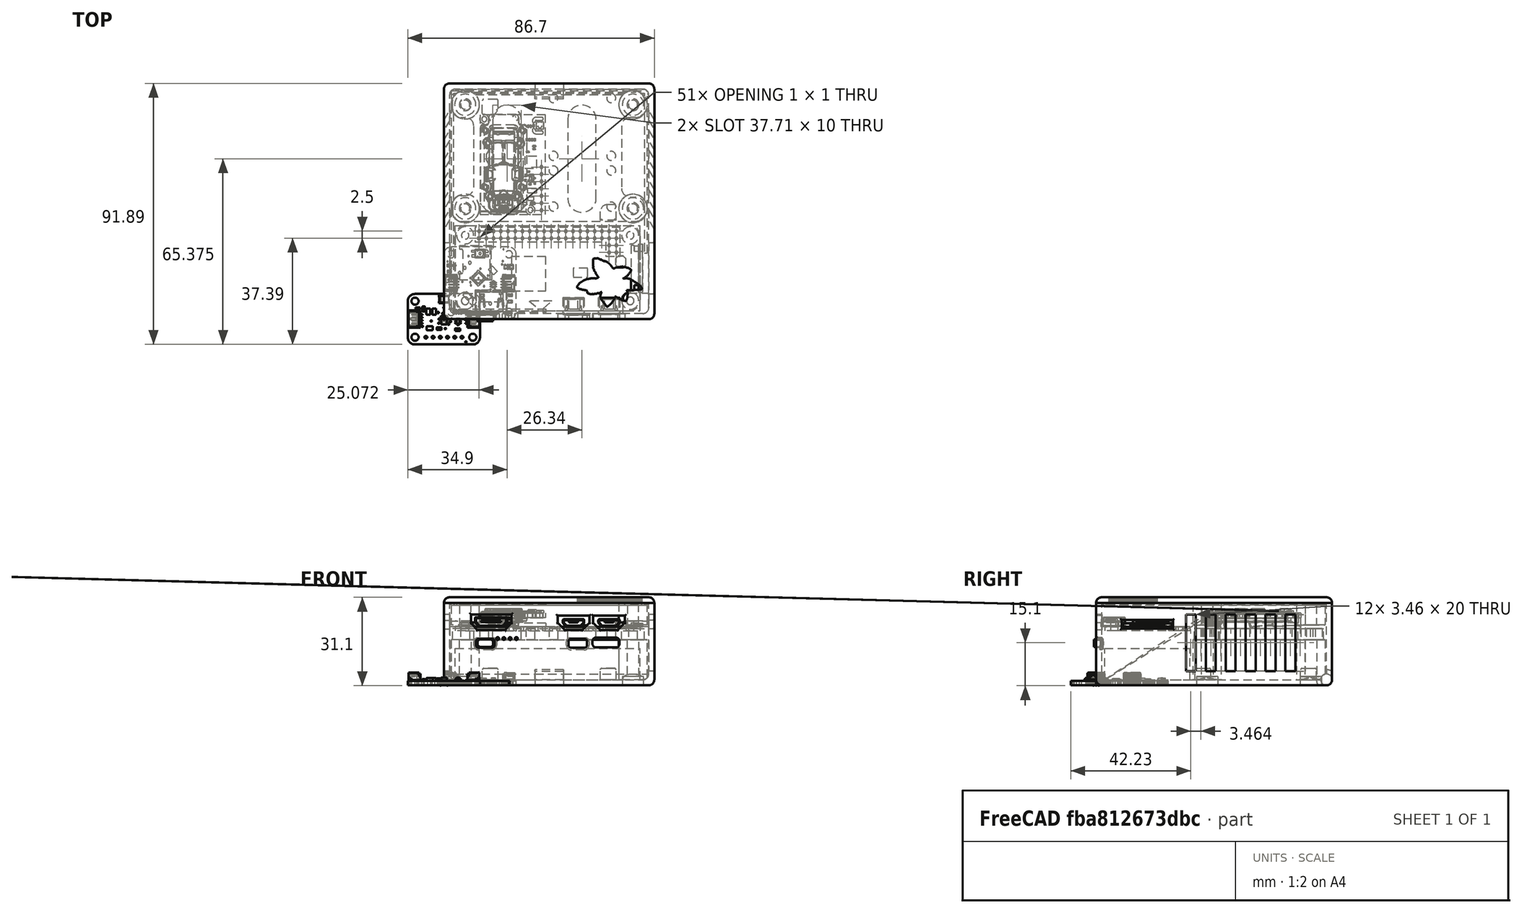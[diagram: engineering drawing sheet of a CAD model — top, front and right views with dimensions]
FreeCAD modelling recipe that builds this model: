
FCSTD DOCUMENT  (FreeCAD 0.20R29410 (Git))
Label: wearableV5_May_1_m3_2023
License: All rights reserved
LicenseURL: http://en.wikipedia.org/wiki/All_rights_reserved
objects: Part::Feature×60, Part::Cylinder×20, Part::MultiFuse×17, Sketcher::SketchObject×15, Part::Extrusion×14, App::Part×9, Part::Fillet×7, Part::Box×4, Part::Cut×4, Mesh::Feature×2, Part::Compound×1
note: 142 computed .brp shape members not serialized (recipe doc carries the construction recipe); baked Part::Feature solids carry a one-line shape summary decoded from their .brp

FEATURE [Part::Box] Box  label="battery"
  AttacherType = Attacher::AttachEngine3D
  Height = 11
  Length = 65
  Placement = pos=(4,3,2) rot=(0,0,1;0rad)
  Width = 30
FEATURE [Mesh::Feature] pisugar3Board
  Placement = pos=(-2.89,36.08,0.25) rot=(-1,0,0;4.71239rad)
FEATURE [Part::Feature] Part__Feature001  label="RaspberryPiZeroW"
  Placement = pos=(36.5,18,19.18) rot=(1,0,0;1.5708rad)
  shape: bbox 65.9 x 31.25 x 4.8 mm, 368 faces, 2 solids (baked)
FEATURE [Part::Feature] Part__Feature  label="ips7100"
  Placement = pos=(-24,0,222) rot=(0.999993,-0.003655,0;3.14159rad)
  shape: bbox 48.14 x 14.05 x 44.14 mm, 1935 faces (baked)
FEATURE [Part::Compound] Compound  label="ips7100s"
  Links = -> [Part__Feature]
  Placement = pos=(13.15,34,15.79) rot=(0,0.707107,0.707107;3.15032rad)
FEATURE [Part::Feature] Part__Feature002  label="Printed Circuit Board"
  shape: bbox 25.4 x 17.78 x 1.6 mm, 42 faces (baked)
FEATURE [Part::Feature] Part__Feature003  label="EAHC2835WD6"
  shape: bbox 3.513 x 2.813 x 0.7485 mm, 108 faces, 4 solids (baked)
FEATURE [Part::Feature] Part__Feature004  label="AS7341 v2"
  Placement = pos=(0,-0.339822,1.6) rot=(0,0,1;0rad)
  shape: bbox 2 x 3.1 x 1.1 mm, 267 faces, 26 solids (baked)
FEATURE [Part::Feature] Part__Feature005  label="CAPC-0805-T0.95-BN v1"
  Placement = pos=(-5.01759,-3.15294,1.6) rot=(0,0,1;0rad)
  shape: bbox 2.1 x 1.35 x 0.95 mm, 42 faces (baked)
FEATURE [Part::Feature] Part__Feature006  label="CAPC-0805-T0.95-BN v002"
  Placement = pos=(-5.48627,2.66154,1.6) rot=(0,0,-1;1.5708rad)
  shape: bbox 1.35 x 2.1 x 0.95 mm, 42 faces (baked)
FEATURE [Part::Feature] Part__Feature007  label="CAPC-0805-T0.95-BN v003"
  Placement = pos=(-3.43627,2.66154,1.6) rot=(0,0,-1;1.5708rad)
  shape: bbox 1.35 x 2.1 x 0.95 mm, 42 faces (baked)
FEATURE [Part::Feature] Part__Feature008  label="CAPC-0603-T0.9-BN v1"
  Placement = pos=(-1.69987,-3.28475,1.6) rot=(0,0,1;0rad)
  shape: bbox 1.7 x 0.9 x 0.9 mm, 42 faces (baked)
FEATURE [Part::Feature] Part__Feature009  label="BODY_MF06A"
  Placement = pos=(0,0,0.762) rot=(0.57735,-0.57735,-0.57735;2.0944rad)
  shape: bbox 1.601 x 2.921 x 1.016 mm, 42 faces (baked)
FEATURE [Part::Feature] Part__Feature010  label="LEAD_MF06A"
  Placement = pos=(-0.9652,-0.9525,0.1016) rot=(0.57735,-0.57735,-0.57735;2.0944rad)
  shape: bbox 0.6223 x 0.3749 x 0.8636 mm, 14 faces (baked)
FEATURE [Part::Feature] Part__Feature011  label="LEAD_MF06A001"
  Placement = pos=(-0.9652,0,0.1016) rot=(0.57735,-0.57735,-0.57735;2.0944rad)
  shape: bbox 0.6223 x 0.3749 x 0.8636 mm, 14 faces (baked)
FEATURE [Part::Feature] Part__Feature012  label="LEAD_MF06A002"
  Placement = pos=(-0.9652,0.9525,0.1016) rot=(0.57735,-0.57735,-0.57735;2.0944rad)
  shape: bbox 0.6223 x 0.3749 x 0.8636 mm, 14 faces (baked)
FEATURE [Part::Feature] Part__Feature013  label="LEAD_MF06A003"
  Placement = pos=(0.9652,-0.9525,0.1016) rot=(0.57735,0.57735,0.57735;2.0944rad)
  shape: bbox 0.6223 x 0.3749 x 0.8636 mm, 14 faces (baked)
FEATURE [Part::Feature] Part__Feature014  label="LEAD_MF06A004"
  Placement = pos=(0.9652,0,0.1016) rot=(0.57735,0.57735,0.57735;2.0944rad)
  shape: bbox 0.6223 x 0.3749 x 0.8636 mm, 14 faces (baked)
FEATURE [Part::Feature] Part__Feature015  label="LEAD_MF06A005"
  Placement = pos=(0.9652,0.9525,0.1016) rot=(0.57735,0.57735,0.57735;2.0944rad)
  shape: bbox 0.6223 x 0.3749 x 0.8636 mm, 14 faces (baked)
FEATURE [Part::Feature] Part__Feature016  label="SOT363 v2"
  Placement = pos=(4.97054,-0.645171,1.675) rot=(0,0,1;3.14159rad)
  shape: bbox 2.1 x 2 x 1.1 mm, 94 faces, 7 solids (baked)
FEATURE [Part::Feature] Part__Feature017  label="LED 0603 single color v1"
  Placement = pos=(-9.18406,3.72778,1.60762) rot=(0,0,1;1.5708rad)
  shape: bbox 1.961 x 0.7932 x 0.7145 mm, 63 faces, 5 solids (baked)
FEATURE [Part::Feature] Part__Feature018  label="RESC-0603 v1"
  Placement = pos=(4.83432,-3.67461,1.6) rot=(0,0,1;0rad)
  shape: bbox 1.7 x 0.9 x 0.55 mm, 52 faces, 3 solids (baked)
FEATURE [Part::Feature] Part__Feature019  label="RESC-0603 v002"
  Placement = pos=(-7.14949,3.61248,1.6) rot=(0,0,-1;1.5708rad)
  shape: bbox 0.9 x 1.7 x 0.55 mm, 52 faces, 3 solids (baked)
FEATURE [Part::Feature] Part__Feature020  label="YC164_RESPACK v1"
  Placement = pos=(2.99591,1.52916,1.6) rot=(0,0,1;0rad)
  shape: bbox 3.2 x 1.6 x 0.61 mm, 172 faces (baked)
FEATURE [Part::Feature] Part__Feature021  label="qwicc v2"
  Placement = pos=(-10.8364,0.0607456,1.65) rot=(0,0,-1;1.5708rad)
  shape: bbox 4.95 x 6 x 2.96 mm, 229 faces, 7 solids (baked)
FEATURE [Part::Feature] Part__Feature022  label="qwicc v003"
  Placement = pos=(10.8256,0.00556102,1.65) rot=(0,0,1;1.5708rad)
  shape: bbox 4.95 x 6 x 2.96 mm, 229 faces, 7 solids (baked)
FEATURE [Part::Feature] Part__Feature023  label="scd30"
  Placement = pos=(21,53,27) rot=(0.57735,0.57735,-0.57735;4.18879rad)
  shape: bbox 23.02 x 35.11 x 7.027 mm, 2292 faces, 25 solids (baked)
FEATURE [App::Part] sot_23_6_v2  label="sot-23-6 v2"
  Group = -> [Part__Feature009,Part__Feature010,Part__Feature011,Part__Feature012,Part__Feature013,Part__Feature014,Part__Feature015]
  Origin = -> Origin
  Placement = pos=(-4.47945,-0.603742,1.69152) rot=(0,0,1;0rad)
FEATURE [App::Part] Adafruit_AS7341_STEMMA_QT_v2  label="bme280"
  Group = -> [Part__Feature002,Part__Feature003,Part__Feature004,Part__Feature005,Part__Feature006,Part__Feature007,Part__Feature008,sot_23_6_v2,Part__Feature016,Part__Feature017,Part__Feature018,Part__Feature019,Part__Feature020,Part__Feature021,Part__Feature022]
  Origin = -> Origin001
  Placement = pos=(48.7,46,20) rot=(0,0,1;0rad)
FEATURE [Part::Box] Box002  label="bottom"
  AttacherType = Attacher::AttachEngine3D
  Height = 29
  Length = 74
  Width = 83
FEATURE [Part::Fillet] Fillet  label="bottom002"
  Base = -> Box002
  Edges = 8 edges r=2: [Edge1,Edge3,Edge4,Edge5,Edge7,Edge8,Edge9,Edge11]
FEATURE [Part::Box] Box003  label="bottom001"
  AttacherType = Attacher::AttachEngine3D
  Height = 39
  Length = 70
  Placement = pos=(2,2,2) rot=(0,0,1;0rad)
  Width = 79
FEATURE [Part::Fillet] Fillet001  label="bottomCut"
  Base = -> Box003
  Edges = 8 edges r=2: [Edge1,Edge3,Edge4,Edge5,Edge7,Edge8,Edge9,Edge11]
FEATURE [Part::Cut] Cut  label="bottom003"
  Base = -> Fillet
  Tool = -> Fillet001
FEATURE [Part::Cylinder] Cylinder
  Angle = 360
  AttacherType = Attacher::AttachEngine3D
  FirstAngle = 0
  Height = 14
  Placement = pos=(7.5,75.5,2) rot=(0,0,1;0rad)
  Radius = 5
  SecondAngle = 0
FEATURE [Part::Cylinder] Cylinder001
  Angle = 360
  AttacherType = Attacher::AttachEngine3D
  FirstAngle = 0
  Height = 14
  Placement = pos=(66.5,39,2) rot=(0,0,1;0rad)
  Radius = 5
  SecondAngle = 0
FEATURE [Part::Cylinder] Cylinder002
  Angle = 360
  AttacherType = Attacher::AttachEngine3D
  FirstAngle = 0
  Height = 14
  Placement = pos=(7.5,39,2) rot=(0,0,1;0rad)
  Radius = 5
  SecondAngle = 0
FEATURE [Part::Cylinder] Cylinder003
  Angle = 360
  AttacherType = Attacher::AttachEngine3D
  FirstAngle = 0
  Height = 14
  Placement = pos=(66.5,75.5,2) rot=(0,0,1;0rad)
  Radius = 5
  SecondAngle = 0
FEATURE [Part::MultiFuse] Fusion  label="basesBottomInDone"
  Shapes = -> [Cylinder003,Cylinder,Cylinder001,Cylinder002]
FEATURE [Part::Feature] Part__Feature024  label="Board"
  shape: bbox 25.4 x 25.4 x 1.57 mm, 211 faces (baked)
FEATURE [Part::Feature] Part__Feature025  label="QFN24_4MM"
  Placement = pos=(12.1412,14.4526,1.57) rot=(0,0,1;3.92699rad)
  shape: bbox 5.657 x 5.657 x 0.9 mm, 172 faces (baked)
FEATURE [Part::Feature] Part__Feature026  label="Part 5"
  shape: bbox 0.48 x 0.6603 x 0.6 mm, 14 faces (baked)
FEATURE [Part::Feature] Part__Feature027  label="Part 6"
  shape: bbox 0.48 x 0.6603 x 0.6 mm, 14 faces (baked)
FEATURE [Part::Feature] Part__Feature028  label="Part 4"
  shape: bbox 0.48 x 0.6603 x 0.6 mm, 14 faces (baked)
FEATURE [Part::Feature] Part__Feature029  label="Part 3"
  shape: bbox 0.48 x 0.6603 x 0.6 mm, 14 faces (baked)
FEATURE [Part::Feature] Part__Feature030  label="Part 2"
  shape: bbox 0.48 x 0.6603 x 0.6 mm, 14 faces (baked)
FEATURE [Part::Feature] Part__Feature031  label="Part 1"
  shape: bbox 3 x 1.4 x 1 mm, 10 faces (baked)
FEATURE [App::Part] _6700497  label="36700497"
  Group = -> [Part__Feature026,Part__Feature027,Part__Feature028,Part__Feature029,Part__Feature030,Part__Feature031]
  Origin = -> Origin002
  Placement = pos=(0,0,0) rot=(0,0,1;3.14159rad)
FEATURE [App::Part] SOT23_5  label="SOT23-5"
  Group = -> [_6700497]
  Origin = -> Origin003
  Placement = pos=(2.54,6.985,1.57) rot=(0,0,1;3.14159rad)
FEATURE [Part::Feature] Part__Feature032  label="Pin1"
  shape: bbox 0.6224 x 1.252 x 1.252 mm, 37 faces (baked)
FEATURE [Part::Feature] Part__Feature033  label="Pin2"
  shape: bbox 0.6224 x 1.252 x 1.252 mm, 37 faces (baked)
FEATURE [Part::Feature] Part__Feature034  label="CeramicBody"
  shape: bbox 1.8 x 1.23 x 1.23 mm, 10 faces (baked)
FEATURE [App::Part] _603_NO  label="0603-NO"
  Group = -> [Part__Feature032,Part__Feature033,Part__Feature034]
  Origin = -> Origin004
  Placement = pos=(16.51,8.382,1.57) rot=(0,0,1;0rad)
FEATURE [Part::Feature] Part__Feature035  label="0603-NO (1)"
  Placement = pos=(23.241,6.223,1.57) rot=(0,0,1;0rad)
  shape: bbox 1.7 x 0.9 x 0.55 mm, 52 faces, 3 solids (baked)
FEATURE [Part::Feature] Part__Feature036  label="0603-NO (2)"
  Placement = pos=(13.3858,8.4328,1.57) rot=(0,0,1;0rad)
  shape: bbox 1.7 x 0.9 x 0.55 mm, 52 faces, 3 solids (baked)
FEATURE [Part::Feature] Part__Feature037  label="0603-NO (3)"
  Placement = pos=(1.905,18.923,1.57) rot=(0,0,1;3.14159rad)
  shape: bbox 1.7 x 0.9 x 0.55 mm, 52 faces, 3 solids (baked)
FEATURE [Part::Feature] Part__Feature038  label="Pin1 (1)"
  shape: bbox 0.6224 x 1.252 x 1.252 mm, 37 faces (baked)
FEATURE [Part::Feature] Part__Feature039  label="Pin2 (1)"
  shape: bbox 0.6224 x 1.252 x 1.252 mm, 37 faces (baked)
FEATURE [Part::Feature] Part__Feature040  label="CeramicBody (1)"
  shape: bbox 1.8 x 1.23 x 1.23 mm, 10 faces (baked)
FEATURE [App::Part] _805_NO  label="0805-NO"
  Group = -> [Part__Feature038,Part__Feature039,Part__Feature040]
  Origin = -> Origin005
  Placement = pos=(7.874,13.589,1.57) rot=(0,0,1;1.5708rad)
FEATURE [Part::Feature] Part__Feature041  label="Pin1 (2)"
  shape: bbox 0.6224 x 1.252 x 1.252 mm, 37 faces (baked)
FEATURE [Part::Feature] Part__Feature042  label="Pin2 (2)"
  shape: bbox 0.6224 x 1.252 x 1.252 mm, 37 faces (baked)
FEATURE [Part::Feature] Part__Feature043  label="CeramicBody (2)"
  shape: bbox 1.8 x 1.23 x 1.23 mm, 10 faces (baked)
FEATURE [App::Part] _805_NO__1_  label="0805-NO (1)"
  Group = -> [Part__Feature041,Part__Feature042,Part__Feature043]
  Origin = -> Origin006
  Placement = pos=(12.827,6.223,1.57) rot=(0,0,1;3.14159rad)
FEATURE [Part::Feature] Part__Feature044  label="CHIPLED_0603_NOOUTLINE"
  Placement = pos=(23.368,8.509,1.57) rot=(0,0,1;1.5708rad)
  shape: bbox 1.616 x 0.8 x 0.4 mm, 133 faces (baked)
FEATURE [Part::Feature] Part__Feature045  label="CHIPLED_0603_NOOUTLINE (1)"
  Placement = pos=(1.905,16.764,1.57) rot=(0,0,-1;1.5708rad)
  shape: bbox 1.616 x 0.8 x 0.4 mm, 133 faces (baked)
FEATURE [Part::Feature] Part__Feature046  label="JST_SH4"
  Placement = pos=(22.86,12.7,1.57) rot=(0,0,1;1.5708rad)
  shape: bbox 4.95 x 6 x 2.96 mm, 229 faces, 7 solids (baked)
FEATURE [Part::Feature] Part__Feature047  label="JST_SH4 (1)"
  Placement = pos=(2.54,12.7,1.57) rot=(0,0,-1;1.5708rad)
  shape: bbox 4.95 x 6 x 2.96 mm, 229 faces, 7 solids (baked)
FEATURE [Part::Feature] Part__Feature048  label="NEO3535_REVERSE"
  Placement = pos=(12.7,23.114,0) rot=(0,1,0;3.14159rad)
  shape: bbox 5.88 x 2.8 x 1.78 mm, 41 faces, 5 solids (baked)
FEATURE [Part::Feature] Part__Feature049  label="RESPACK_4X0603"
  Placement = pos=(22.86,18.415,1.57) rot=(0,0,1;3.14159rad)
  shape: bbox 3.2 x 1.6 x 0.61 mm, 172 faces (baked)
FEATURE [Part::Feature] Part__Feature050  label="SOT363"
  Placement = pos=(17.399,12.192,1.57) rot=(0,0,-1;1.5708rad)
  shape: bbox 2.208 x 2.208 x 1.121 mm, 178 faces, 4 solids (baked)
FEATURE [App::Part] Packages
  Group = -> [Part__Feature025,SOT23_5,_603_NO,Part__Feature035,Part__Feature036,Part__Feature037,_805_NO,_805_NO__1_,Part__Feature044,Part__Feature045,Part__Feature046,Part__Feature047,Part__Feature048,Part__Feature049,Part__Feature050]
  Origin = -> Origin007
FEATURE [App::Part] Adafruit_I2C_QT_Rotary_Encoder_v2  label="gps"
  Group = -> [Part__Feature024,Packages]
  Origin = -> Origin008
  Placement = pos=(36,55,20) rot=(0,0,1;0rad)
FEATURE [Part::Cylinder] Cylinder004
  Angle = 360
  AttacherType = Attacher::AttachEngine3D
  FirstAngle = 0
  Height = 14
  Placement = pos=(7.5,75.5,2) rot=(0,0,1;0rad)
  Radius = 2.1
  SecondAngle = 0
FEATURE [Part::Cylinder] Cylinder005
  Angle = 360
  AttacherType = Attacher::AttachEngine3D
  FirstAngle = 0
  Height = 14
  Placement = pos=(66.5,39,2) rot=(0,0,1;0rad)
  Radius = 2.1
  SecondAngle = 0
FEATURE [Part::Cylinder] Cylinder006
  Angle = 360
  AttacherType = Attacher::AttachEngine3D
  FirstAngle = 0
  Height = 14
  Placement = pos=(7.5,39,2) rot=(0,0,1;0rad)
  Radius = 2.1
  SecondAngle = 0
FEATURE [Part::Cylinder] Cylinder007
  Angle = 360
  AttacherType = Attacher::AttachEngine3D
  FirstAngle = 0
  Height = 14
  Placement = pos=(66.5,75.5,2) rot=(0,0,1;0rad)
  Radius = 2.1
  SecondAngle = 0
FEATURE [Part::MultiFuse] Fusion001  label="basesM4BottomCutsDone"
  Shapes = -> [Cylinder007,Cylinder004,Cylinder005,Cylinder006]
FEATURE [Sketcher::SketchObject] Sketch
  FullyConstrained = true
  sketch-geometry (39):
    g0: LineSegment StartX=3 StartY=43.5 StartZ=0 EndX=3 EndY=34.5 EndZ=0
    g1: LineSegment StartX=3 StartY=34.5 StartZ=0 EndX=70.5 EndY=34.5 EndZ=0
    g2: LineSegment StartX=3 StartY=43.5 StartZ=0 EndX=10.5 EndY=43.5 EndZ=0
    g3: LineSegment StartX=3 StartY=71 StartZ=0 EndX=10.5 EndY=71 EndZ=0
    g4: LineSegment StartX=3 StartY=71 StartZ=0 EndX=3 EndY=80 EndZ=0
    g5: LineSegment StartX=70.5 StartY=80 StartZ=0 EndX=70.5 EndY=71 EndZ=0
    g6: LineSegment StartX=70.5 StartY=71 StartZ=0 EndX=62.5 EndY=71 EndZ=0
    g7: LineSegment StartX=62.5 StartY=71 StartZ=0 EndX=62.5 EndY=43 EndZ=0
    g8: LineSegment StartX=62.5 StartY=43 StartZ=0 EndX=70.5 EndY=43 EndZ=0
    g9: LineSegment StartX=70.5 StartY=43 StartZ=0 EndX=70.5 EndY=34.5 EndZ=0
    g10: GeomPoint X=70.5 Y=34.5 Z=0
    g11: GeomPoint X=70.5 Y=34.5 Z=0
    g12: GeomPoint X=70.5 Y=34.5 Z=0
    g13: GeomPoint X=70.5 Y=34.5 Z=0
    g14: GeomPoint X=70.5 Y=34.5 Z=0
    g15: LineSegment StartX=10.5 StartY=43.5 StartZ=0 EndX=10.5 EndY=71 EndZ=0
    g16: Circle CenterX=7.5 CenterY=75.5 CenterZ=0 NormalX=0 NormalY=0 NormalZ=1 AngleXU=0 Radius=1.6
    g17: Circle CenterX=7.5 CenterY=39 CenterZ=0 NormalX=0 NormalY=0 NormalZ=1 AngleXU=0 Radius=1.6
    g18: Circle CenterX=66.5 CenterY=39 CenterZ=0 NormalX=0 NormalY=0 NormalZ=1 AngleXU=0 Radius=1.6
    g19: Circle CenterX=66.5 CenterY=75.5 CenterZ=0 NormalX=0 NormalY=0 NormalZ=1 AngleXU=0 Radius=1.6
    g20: Circle CenterX=14.2 CenterY=70.46 CenterZ=0 NormalX=0 NormalY=0 NormalZ=1 AngleXU=0 Radius=1.6
    g21: Circle CenterX=38.54 CenterY=77.84 CenterZ=0 NormalX=0 NormalY=0 NormalZ=1 AngleXU=0 Radius=1.6
    g22: Circle CenterX=58.86 CenterY=77.84 CenterZ=0 NormalX=0 NormalY=0 NormalZ=1 AngleXU=0 Radius=1.6
    g23: Circle CenterX=38.54 CenterY=57.52 CenterZ=0 NormalX=0 NormalY=0 NormalZ=1 AngleXU=0 Radius=1.6
    g24: Circle CenterX=58.86 CenterY=57.52 CenterZ=0 NormalX=0 NormalY=0 NormalZ=1 AngleXU=0 Radius=1.6
    g25: Circle CenterX=38.54 CenterY=52.33 CenterZ=0 NormalX=0 NormalY=0 NormalZ=1 AngleXU=0 Radius=1.6
    g26: Circle CenterX=58.86 CenterY=52.33 CenterZ=0 NormalX=0 NormalY=0 NormalZ=1 AngleXU=0 Radius=1.6
    g27: Circle CenterX=38.54 CenterY=39.63 CenterZ=0 NormalX=0 NormalY=0 NormalZ=1 AngleXU=0 Radius=1.6
    g28: Circle CenterX=58.86 CenterY=39.63 CenterZ=0 NormalX=0 NormalY=0 NormalZ=1 AngleXU=0 Radius=1.6
    g29: Circle CenterX=30.43 CenterY=38.46 CenterZ=0 NormalX=0 NormalY=0 NormalZ=1 AngleXU=0 Radius=1.6
    g30: ArcOfCircle CenterX=48.54 CenterY=70.34 CenterZ=0 NormalX=0 NormalY=0 NormalZ=1 AngleXU=0 Radius=5 StartAngle=-9e-16 EndAngle=3.14159
    g31: ArcOfCircle CenterX=48.54 CenterY=42.63 CenterZ=0 NormalX=0 NormalY=0 NormalZ=1 AngleXU=0 Radius=5 StartAngle=3.14159 EndAngle=6.28319
    g32: LineSegment StartX=43.54 StartY=70.34 StartZ=0 EndX=43.54 EndY=42.63 EndZ=0
    g33: LineSegment StartX=53.54 StartY=42.63 StartZ=0 EndX=53.54 EndY=70.34 EndZ=0
    g34: ArcOfCircle CenterX=22.2 CenterY=70.34 CenterZ=0 NormalX=0 NormalY=0 NormalZ=1 AngleXU=0 Radius=5 StartAngle=0 EndAngle=3.14159
    g35: ArcOfCircle CenterX=22.2 CenterY=42.63 CenterZ=0 NormalX=0 NormalY=0 NormalZ=1 AngleXU=0 Radius=5 StartAngle=3.14159 EndAngle=6.28319
    g36: LineSegment StartX=17.2 StartY=70.34 StartZ=0 EndX=17.2 EndY=42.63 EndZ=0
    g37: LineSegment StartX=27.2 StartY=42.63 StartZ=0 EndX=27.2 EndY=70.34 EndZ=0
    g38: LineSegment StartX=3 StartY=80 StartZ=0 EndX=70.5 EndY=80 EndZ=0
  constraints (103):
    c: Vertical(g0)
    c: Coincident(g1,g0)
    c: Horizontal(g1)
    c: Coincident(g2,g0)
    c: Coincident(g4,g3)
    c: Vertical(g4)
    c: Coincident(g6,g5)
    c: Horizontal(g6)
    c: Coincident(g7,g6)
    c: Vertical(g7)
    c: Horizontal(g8)
    c: Horizontal(g2)
    c: Coincident(g10,g9)
    c: Coincident(g11,g1)
    c: Coincident(g12,g9)
    c: Coincident(g13,g1)
    c: Coincident(g14,g9)
    c: Coincident(g9,g1)
    c: Vertical(g9)
    c: Coincident(g15,g2)
    c: Coincident(g15,g3)
    c: Vertical(g15)
    c: Horizontal(g3)
    c: Vertical(g5)
    c: Coincident(g8,g9)
    c: Coincident(g7,g8)
    c: DistanceX(g8,g8) = 8
    c: Radius(g16) = 1.6
    c: DistanceY(g17) = 39
    c: Radius(g17) = 1.6
    c: DistanceX(g18) = 66.5
    c: DistanceY(g17,g18) = 0
    c: Radius(g18) = 1.6
    c: DistanceX(g19,g18) = 0
    c: Radius(g19) = 1.6
    c: DistanceY(g16) = 75.5
    c: DistanceY(g16,g19) = 0
    c: DistanceY(g3,g5) = 0
    c: Radius(g21) = 1.6
    c: DistanceY(g21,g22) = 0
    c: Radius(g22) = 1.6
    c: DistanceX(g21,g22) = 20.32
    c: DistanceX(g23,g21) = 0
    c: Radius(g23) = 1.6
    c: DistanceY(g23,g21) = 20.32
    c: DistanceY(g24,g23) = 0
    c: DistanceX(g24,g22) = 0
    c: Radius(g24) = 1.6
    c: DistanceX(g25,g23) = 0
    c: Radius(g25) = 1.6
    c: DistanceY(g25,g26) = 0
    c: DistanceX(g24,g26) = 0
    c: Radius(g26) = 1.6
    c: DistanceX(g25,g27) = 0
    c: DistanceX(g28,g26) = 0
    c: DistanceY(g27,g25) = 12.7
    c: DistanceY(g28,g27) = 0
    c: Radius(g28) = 1.6
    c: Radius(g27) = 1.6
    c: Radius(g29) = 1.6
    c: DistanceY(g29,g20) = 32
    c: Radius(g20) = 1.6
    c: Tangent(g30,g32) = -1.5708
    c: Tangent(g32,g31) = -1.5708
    c: Tangent(g31,g33) = -1.5708
    c: Tangent(g33,g30) = -1.5708
    c: Equal(g30,g31)
    c: Vertical(g32)
    c: DistanceY(g27,g31) = 3
    c: Radius(g30) = 5
    c: Tangent(g34,g36) = -1.5708
    c: Tangent(g36,g35) = -1.5708
    c: Tangent(g35,g37) = -1.5708
    c: Tangent(g37,g34) = -1.5708
    c: Equal(g34,g35)
    c: Vertical(g36)
    c: Radius(g34) = 5
    c: DistanceY(g34,g30) = 0
    c: DistanceY(g31,g35) = 0
    c: DistanceX(g16,g17) = 0
    c: DistanceX(g0,g3) = 0
    c: Coincident(g38,g4)
    c: Coincident(g38,g5)
    c: Horizontal(g38)
    c: DistanceX(g29) = 30.43
    c: DistanceX(g20) = 14.2
    c: DistanceY(g20) = 70.46
    c: DistanceX(g27) = 38.54
    c: DistanceY(g27) = 39.63
    c: DistanceY(g23) = 57.52
    c: DistanceY(g3,g16) = 4.5
    c: DistanceY(g16,g4) = 4.5
    c: DistanceY(g0,g17) = 4.5
    c: DistanceX(g0,g17) = 4.5
    c: DistanceX(g17) = 7.5
    c: DistanceY(g17,g0) = 4.5
    c: DistanceX(g16,g3) = 3
    c: DistanceX(g19,g5) = 4
    c: DistanceX(g6,g19) = 4
    c: DistanceY(g18,g8) = 4
    c: DistanceX(g25,g31) = 10
    c: DistanceY(g30,g21) = 7.5
    c: DistanceX(g20,g34) = 8
FEATURE [Part::Extrusion] Extrude  label="sensorHold"
  Base = -> Sketch
  Dir = (0,0,1)
  DirMode = 2
  FaceMakerClass = Part::FaceMakerBullseye
  LengthFwd = 4
  LengthRev = 0
  Placement = pos=(0,0,16) rot=(0,0,1;0rad)
  Solid = true
  Symmetric = false
FEATURE [Part::Fillet] Fillet002  label="sensorHold001"
  Base = -> Extrude
  Edges = 12 edges r=3: [Edge1,Edge2,Edge5,Edge8,Edge11,Edge14,Edge17,Edge20,Edge23,Edge26,Edge29,Edge32]
FEATURE [Sketcher::SketchObject] Sketch001
  FullyConstrained = true
  sketch-geometry (10):
    g0: LineSegment StartX=19.03 StartY=74.44 StartZ=0 EndX=19.03 EndY=77.44 EndZ=0
    g1: LineSegment StartX=16.53 StartY=71.94 StartZ=0 EndX=13.53 EndY=71.94 EndZ=0
    g2: LineSegment StartX=13.53 StartY=71.94 StartZ=0 EndX=13.53 EndY=77.44 EndZ=0
    g3: LineSegment StartX=19.03 StartY=77.44 StartZ=0 EndX=13.53 EndY=77.44 EndZ=0
    g4: ArcOfCircle CenterX=16.53 CenterY=74.44 CenterZ=0 NormalX=0 NormalY=0 NormalZ=1 AngleXU=0 Radius=2.5 StartAngle=4.71239 EndAngle=6.28319
    g5: LineSegment StartX=60.53 StartY=34.86 StartZ=0 EndX=55.03 EndY=34.86 EndZ=0
    g6: LineSegment StartX=55.03 StartY=34.86 StartZ=0 EndX=55.03 EndY=37.86 EndZ=0
    g7: LineSegment StartX=60.53 StartY=34.86 StartZ=0 EndX=60.53 EndY=40.36 EndZ=0
    g8: LineSegment StartX=60.53 StartY=40.36 StartZ=0 EndX=57.53 EndY=40.36 EndZ=0
    g9: ArcOfCircle CenterX=57.53 CenterY=37.86 CenterZ=0 NormalX=0 NormalY=0 NormalZ=1 AngleXU=0 Radius=2.5 StartAngle=1.5708 EndAngle=3.14159
  constraints (32):
    c: Vertical(g0)
    c: Horizontal(g1)
    c: Vertical(g2)
    c: Coincident(g2,g3)
    c: Coincident(g0,g3)
    c: Horizontal(g3)
    c: DistanceX(g3,g3) = 5.5
    c: DistanceY(g2,g2) = 5.5
    c: DistanceY(g4,g4) = 0
    c: DistanceX(g4,g4) = 0
    c: Coincident(g1,g4)
    c: Coincident(g0,g4)
    c: Radius(g4) = 2.5
    c: DistanceX(g4) = 16.53
    c: DistanceY(g4) = 74.44
    c: Coincident(g1,g2)
    c: Horizontal(g5)
    c: Vertical(g6)
    c: Vertical(g7)
    c: Horizontal(g8)
    c: Coincident(g7,g8)
    c: Coincident(g8,g9)
    c: Coincident(g6,g9)
    c: Coincident(g5,g6)
    c: Coincident(g5,g7)
    c: DistanceX(g5,g5) = 5.5
    c: DistanceY(g7,g7) = 5.5
    c: DistanceY(g6,g6) = 3
    c: DistanceX(g8,g8) = 3
    c: Radius(g9) = 2.5
    c: DistanceY(g9,g4) = 36.58
    c: DistanceX(g4,g9) = 41
FEATURE [Part::Extrusion] Extrude001
  Base = -> Sketch001
  Dir = (0,0,1)
  DirMode = 2
  FaceMakerClass = Part::FaceMakerBullseye
  LengthFwd = 4
  LengthRev = 0
  Placement = pos=(0,0,2) rot=(0,0,1;0rad)
  Solid = true
  Symmetric = false
FEATURE [Part::Fillet] Fillet003  label="ipsHoldBottomInDone"
  Base = -> Extrude001
  Edges = 14 edges r=0.5: [Edge4,Edge7,Edge10,Edge11,Edge13,Edge15,Edge19,Edge20,Edge22,Edge23,Edge25,Edge26,Edge28,Edge30]
FEATURE [Sketcher::SketchObject] Sketch002
  FullyConstrained = true
  MapMode = 2
  Support = -> [Cut]
  sketch-geometry (10):
    g0: LineSegment StartX=63 StartY=9.25 StartZ=0 EndX=72 EndY=9.25 EndZ=0
    g1: LineSegment StartX=72 StartY=9.25 StartZ=0 EndX=72 EndY=2 EndZ=0
    g2: LineSegment StartX=72 StartY=2 StartZ=0 EndX=63 EndY=2 EndZ=0
    g3: LineSegment StartX=63 StartY=2 StartZ=0 EndX=63 EndY=9.25 EndZ=0
    g4: LineSegment StartX=2 StartY=9.25 StartZ=0 EndX=10 EndY=9.25 EndZ=0
    g5: LineSegment StartX=10 StartY=9.25 StartZ=0 EndX=10 EndY=2 EndZ=0
    g6: LineSegment StartX=10 StartY=2 StartZ=0 EndX=2 EndY=2 EndZ=0
    g7: LineSegment StartX=2 StartY=2 StartZ=0 EndX=2 EndY=9.25 EndZ=0
    g8: Circle CenterX=7.47 CenterY=6.47 CenterZ=0 NormalX=0 NormalY=0 NormalZ=1 AngleXU=0 Radius=1.35
    g9: Circle CenterX=65.52 CenterY=6.47 CenterZ=0 NormalX=0 NormalY=0 NormalZ=1 AngleXU=0 Radius=1.35
  constraints (30):
    c: Coincident(g0,g1)
    c: Coincident(g1,g2)
    c: Coincident(g2,g3)
    c: Coincident(g3,g0)
    c: Horizontal(g0)
    c: Horizontal(g2)
    c: Vertical(g1)
    c: Vertical(g3)
    c: Coincident(g4,g5)
    c: Coincident(g5,g6)
    c: Coincident(g6,g7)
    c: Coincident(g7,g4)
    c: Horizontal(g4)
    c: Horizontal(g6)
    c: Vertical(g5)
    c: Vertical(g7)
    c: DistanceX(g6) = 2
    c: DistanceY(g6) = 2
    c: DistanceX(g6,g6) = 8
    c: DistanceY(g7,g7) = 7.25
    c: DistanceX(g-1,g1) = 72
    c: DistanceY(g2,g5) = 0
    c: DistanceY(g0,g4) = 0
    c: DistanceX(g2,g2) = 9
    c: DistanceX(g8) = 7.47
    c: Radius(g8) = 1.35
    c: DistanceX(g9) = 65.52
    c: DistanceY(g8,g9) = 0
    c: Radius(g9) = 1.35
    c: DistanceY(g8) = 6.47
FEATURE [Part::Extrusion] Extrude002  label="RaberryPiHold"
  Base = -> Sketch002
  Dir = (0,0,1)
  DirMode = 2
  FaceMakerClass = Part::FaceMakerBullseye
  LengthFwd = 2
  LengthRev = 0
  Placement = pos=(0,0,20.7) rot=(0,0,1;0rad)
  Solid = true
  Symmetric = false
FEATURE [Part::Fillet] Fillet004  label="piHoldBottomInDone"
  Base = -> Extrude002
  Edges = 6 edges: [Edge1 r=2,Edge4 r=1,Edge12 r=1,Edge17 r=2,Edge19 r=1,Edge22 r=1]
FEATURE [Part::Box] Box004  label="top"
  AttacherType = Attacher::AttachEngine3D
  Height = 2
  Length = 74
  Placement = pos=(0,0,28) rot=(0,0,1;0rad)
  Width = 83
FEATURE [Part::Fillet] Fillet005  label="top001"
  Base = -> Box004
  Edges = 8 edges r=1.95: [Edge1,Edge2,Edge3,Edge5,Edge6,Edge7,Edge10,Edge12]
FEATURE [Part::Feature] Part__Feature052  label="m4s"
  Placement = pos=(66.5,75.5,14) rot=(1,0,0;3.14159rad)
  shape: bbox 5.501 x 5.501 x 28.29 mm, 108 faces (baked)
FEATURE [Part::Feature] Part__Feature053  label="m4s001"
  Placement = pos=(7.5,75.5,14) rot=(1,0,0;3.14159rad)
  shape: bbox 5.501 x 5.501 x 28.29 mm, 108 faces (baked)
FEATURE [Part::Feature] Part__Feature054  label="m4s002"
  Placement = pos=(66.5,39,14) rot=(1,0,0;3.14159rad)
  shape: bbox 5.501 x 5.501 x 28.29 mm, 108 faces (baked)
FEATURE [Part::Feature] Part__Feature055  label="m4s003"
  Placement = pos=(7.5,39,14) rot=(1,0,0;3.14159rad)
  shape: bbox 5.501 x 5.501 x 28.29 mm, 108 faces (baked)
FEATURE [Part::Cylinder] Cylinder008
  Angle = 360
  AttacherType = Attacher::AttachEngine3D
  FirstAngle = 0
  Height = 7.75
  Placement = pos=(7.5,75.5,2) rot=(0,0,1;0rad)
  Radius = 5
  SecondAngle = 0
FEATURE [Part::Cylinder] Cylinder009
  Angle = 360
  AttacherType = Attacher::AttachEngine3D
  FirstAngle = 0
  Height = 7.75
  Placement = pos=(66.5,39,2) rot=(0,0,1;0rad)
  Radius = 5
  SecondAngle = 0
FEATURE [Part::Cylinder] Cylinder010
  Angle = 360
  AttacherType = Attacher::AttachEngine3D
  FirstAngle = 0
  Height = 7.75
  Placement = pos=(7.5,39,2) rot=(0,0,1;0rad)
  Radius = 5
  SecondAngle = 0
FEATURE [Part::Cylinder] Cylinder011
  Angle = 360
  AttacherType = Attacher::AttachEngine3D
  FirstAngle = 0
  Height = 7.75
  Placement = pos=(66.5,75.5,2) rot=(0,0,1;0rad)
  Radius = 5
  SecondAngle = 0
FEATURE [Part::Feature] Part__Feature056  label="m4Nut"
  Placement = pos=(7.5,39,27) rot=(0,0,1;1.5708rad)
  shape: bbox 8.084 x 8.084 x 2.714 mm, 34 faces (baked)
FEATURE [Part::MultiFuse] Fusion003  label="m4s004"
  Shapes = -> [Part__Feature055,Part__Feature052,Part__Feature053,Part__Feature054]
FEATURE [Part::Feature] Part__Feature057  label="m4Nut001"
  Placement = pos=(66.5,39,27) rot=(0,0,1;1.5708rad)
  shape: bbox 8.084 x 8.084 x 2.714 mm, 34 faces (baked)
FEATURE [Part::MultiFuse] Fusion004
  Shapes = -> [Part__Feature056,Part__Feature057]
FEATURE [Part::Feature] Part__Feature058  label="m4Nut002"
  Placement = pos=(7.5,39,27) rot=(0,0,1;1.5708rad)
  shape: bbox 8.084 x 8.084 x 2.714 mm, 34 faces (baked)
FEATURE [Part::Feature] Part__Feature059  label="m4Nut003"
  Placement = pos=(66.5,39,27) rot=(0,0,1;1.5708rad)
  shape: bbox 8.084 x 8.084 x 2.714 mm, 34 faces (baked)
FEATURE [Part::MultiFuse] Fusion005
  Placement = pos=(0,36.5,0) rot=(0,0,1;0rad)
  Shapes = -> [Part__Feature058,Part__Feature059]
FEATURE [Part::MultiFuse] Fusion006  label="m4Nuts"
  Shapes = -> [Fusion005,Fusion004]
FEATURE [Sketcher::SketchObject] Sketch003
  FullyConstrained = true
  MapMode = 2
  Placement = pos=(70,0,30) rot=(0,1,0;3.14159rad)
  sketch-geometry (36):
    g0: LineSegment StartX=1.125 StartY=35.3194 StartZ=0 EndX=5.375 EndY=35.3194 EndZ=0
    g1: LineSegment StartX=5.375 StartY=35.3194 StartZ=0 EndX=5.47604 EndY=35.4944 EndZ=0
    g2: LineSegment StartX=1.125 StartY=35.3194 StartZ=0 EndX=-1 EndY=39 EndZ=0
    g3: LineSegment StartX=-1 StartY=39 StartZ=0 EndX=1.125 EndY=42.6806 EndZ=0
    g4: LineSegment StartX=1.125 StartY=42.6806 StartZ=0 EndX=5.375 EndY=42.6806 EndZ=0
    g5: LineSegment StartX=5.375 StartY=42.6806 StartZ=0 EndX=5.47604 EndY=42.5056 EndZ=0
    g6: LineSegment StartX=5.47604 StartY=42.5056 StartZ=0 EndX=8.47604 EndY=42.5056 EndZ=0
    g7: LineSegment StartX=8.47604 StartY=42.5056 StartZ=0 EndX=8.47604 EndY=35.4944 EndZ=0
    g8: LineSegment StartX=8.47604 StartY=35.4944 StartZ=0 EndX=5.47604 EndY=35.4944 EndZ=0
    g9: LineSegment StartX=60.524 StartY=35.4944 StartZ=0 EndX=60.625 EndY=35.3194 EndZ=0
    g10: LineSegment StartX=60.625 StartY=35.3194 StartZ=0 EndX=64.875 EndY=35.3194 EndZ=0
    g11: LineSegment StartX=64.875 StartY=35.3194 StartZ=0 EndX=67 EndY=39 EndZ=0
    g12: LineSegment StartX=67 StartY=39 StartZ=0 EndX=64.875 EndY=42.6806 EndZ=0
    g13: LineSegment StartX=64.875 StartY=42.6806 StartZ=0 EndX=60.625 EndY=42.6806 EndZ=0
    g14: LineSegment StartX=60.625 StartY=42.6806 StartZ=0 EndX=60.524 EndY=42.5056 EndZ=0
    g15: LineSegment StartX=60.524 StartY=42.5056 StartZ=0 EndX=57.524 EndY=42.5056 EndZ=0
    g16: LineSegment StartX=57.524 StartY=42.5056 StartZ=0 EndX=57.524 EndY=35.4944 EndZ=0
    g17: LineSegment StartX=57.524 StartY=35.4944 StartZ=0 EndX=60.524 EndY=35.4944 EndZ=0
    g18: LineSegment StartX=-1 StartY=75.5 StartZ=0 EndX=1.125 EndY=71.8194 EndZ=0
    g19: LineSegment StartX=1.125 StartY=71.8194 StartZ=0 EndX=5.375 EndY=71.8194 EndZ=0
    g20: LineSegment StartX=5.375 StartY=71.8194 StartZ=0 EndX=5.47604 EndY=71.9944 EndZ=0
    g21: LineSegment StartX=5.47604 StartY=71.9944 StartZ=0 EndX=8.47604 EndY=71.9944 EndZ=0
    g22: LineSegment StartX=8.47604 StartY=71.9944 StartZ=0 EndX=8.47604 EndY=79.0056 EndZ=0
    g23: LineSegment StartX=8.47604 StartY=79.0056 StartZ=0 EndX=5.47604 EndY=79.0056 EndZ=0
    g24: LineSegment StartX=5.47604 StartY=79.0056 StartZ=0 EndX=5.375 EndY=79.1806 EndZ=0
    g25: LineSegment StartX=5.375 StartY=79.1806 StartZ=0 EndX=1.125 EndY=79.1806 EndZ=0
    g26: LineSegment StartX=1.125 StartY=79.1806 StartZ=0 EndX=-1 EndY=75.5 EndZ=0
    g27: LineSegment StartX=67 StartY=75.5 StartZ=0 EndX=64.875 EndY=71.8194 EndZ=0
    g28: LineSegment StartX=64.875 StartY=71.8194 StartZ=0 EndX=60.625 EndY=71.8194 EndZ=0
    g29: LineSegment StartX=60.625 StartY=71.8194 StartZ=0 EndX=60.524 EndY=71.9944 EndZ=0
    g30: LineSegment StartX=60.524 StartY=71.9944 StartZ=0 EndX=57.524 EndY=71.9944 EndZ=0
    g31: LineSegment StartX=57.524 StartY=71.9944 StartZ=0 EndX=57.524 EndY=79.0056 EndZ=0
    g32: LineSegment StartX=57.524 StartY=79.0056 StartZ=0 EndX=60.524 EndY=79.0056 EndZ=0
    g33: LineSegment StartX=60.524 StartY=79.0056 StartZ=0 EndX=60.625 EndY=79.1806 EndZ=0
    g34: LineSegment StartX=60.625 StartY=79.1806 StartZ=0 EndX=64.875 EndY=79.1806 EndZ=0
    g35: LineSegment StartX=64.875 StartY=79.1806 StartZ=0 EndX=67 EndY=75.5 EndZ=0
  constraints (108):
    c: Horizontal(g0)
    c: Coincident(g1,g0)
    c: Coincident(g2,g0)
    c: Coincident(g4,g3)
    c: Horizontal(g4)
    c: Coincident(g5,g4)
    c: Coincident(g6,g5)
    c: Horizontal(g6)
    c: Coincident(g7,g6)
    c: Vertical(g7)
    c: Coincident(g8,g7)
    c: Coincident(g8,g1)
    c: Angle(g0,g2) = 2.0944
    c: Coincident(g2,g3)
    c: Distance(g2) = 4.25
    c: Distance(g3) = 4.25
    c: DistanceY(g2) = 39
    c: Angle(g3,g4) = 2.0944
    c: DistanceX(g2) = -1
    c: Distance(g4) = 4.25
    c: Distance(g0) = 4.25
    c: Angle(g4,g5) = 2.0944
    c: Angle(g1,g0) = 2.0944
    c: DistanceY(g1,g1) = 0.175
    c: Horizontal(g8)
    c: DistanceX(g8,g8) = 3
    c: Coincident(g10,g9)
    c: Horizontal(g10)
    c: Coincident(g11,g10)
    c: Coincident(g15,g14)
    c: Horizontal(g15)
    c: Coincident(g16,g15)
    c: Vertical(g16)
    c: Coincident(g17,g16)
    c: Coincident(g17,g9)
    c: Horizontal(g17)
    c: Angle(g11,g10) = 2.0944
    c: Angle(g12,g11) = 2.0944
    c: Coincident(g11,g12)
    c: Angle(g13,g12) = 2.0944
    c: Coincident(g13,g14)
    c: Coincident(g12,g13)
    c: Angle(g14,g13) = 2.0944
    c: Angle(g10,g9) = 2.0944
    c: DistanceX(g14,g9) = 0
    c: DistanceX(g13,g9) = 0
    c: Distance(g10) = 4.25
    c: Distance(g11) = 4.25
    c: Distance(g13) = 4.25
    c: DistanceX(g17,g17) = 3
    c: DistanceY(g5,g4) = 0.175
    c: DistanceX(g2,g11) = 68
    c: DistanceY(g11,g2) = 0
    c: DistanceY(g15,g6) = 0
    c: Coincident(g18,g19)
    c: Horizontal(g19)
    c: Coincident(g19,g20)
    c: Coincident(g20,g21)
    c: Horizontal(g21)
    c: Coincident(g21,g22)
    c: Vertical(g22)
    c: Coincident(g22,g23)
    c: Coincident(g23,g24)
    c: Coincident(g24,g25)
    c: Horizontal(g25)
    c: Coincident(g25,g26)
    c: Coincident(g26,g18)
    c: DistanceX(g18,g2) = 0
    c: DistanceY(g2,g18) = 36.5
    c: Angle(g18,g26) = 2.0944
    c: Angle(g26,g25) = 2.0944
    c: Angle(g20,g19) = 2.0944
    c: Angle(g25,g24) = 2.0944
    c: DistanceY(g23,g24) = 0.175
    c: DistanceY(g19,g20) = 0.175
    c: Distance(g21) = 3
    c: Horizontal(g23)
    c: Coincident(g27,g28)
    c: Horizontal(g28)
    c: Coincident(g28,g29)
    c: Coincident(g29,g30)
    c: Horizontal(g30)
    c: Coincident(g30,g31)
    c: Vertical(g31)
    c: Coincident(g31,g32)
    c: Horizontal(g32)
    c: Coincident(g32,g33)
    c: Coincident(g33,g34)
    c: Horizontal(g34)
    c: Coincident(g34,g35)
    c: Coincident(g35,g27)
    c: DistanceX(g11,g27) = 0
    c: DistanceY(g18,g27) = 0
    c: Angle(g27,g28) = 2.0944
    c: Angle(g35,g27) = 2.0944
    c: Angle(g33,g34) = 2.0944
    c: DistanceX(g32,g32) = 3
    c: Angle(g28,g29) = 2.0944
    c: DistanceY(g28,g29) = 0.175
    c: DistanceY(g32,g33) = 0.175
    c: DistanceX(g30,g15) = 0
    c: Distance(g18) = 4.25
    c: Distance(g26) = 4.25
    c: Distance(g19) = 4.25
    c: Distance(g25) = 4.25
    c: Distance(g28) = 4.25
    c: Distance(g27) = 4.25
    c: Distance(g35) = 4.25
FEATURE [Part::Feature] Part__Feature060  label="logoTopCut"
  Placement = pos=(27,-2,35) rot=(-1,0,0;1.5708rad)
  shape: bbox 22.79 x 17.08 x 8 mm, 886 faces (baked)
FEATURE [Part::Cylinder] Cylinder012
  Angle = 360
  AttacherType = Attacher::AttachEngine3D
  FirstAngle = 0
  Height = 3.15
  Placement = pos=(7.5,75.5,2) rot=(0,0,1;0rad)
  Radius = 3.75
  SecondAngle = 0
FEATURE [Part::Cylinder] Cylinder013
  Angle = 360
  AttacherType = Attacher::AttachEngine3D
  FirstAngle = 0
  Height = 3.15
  Placement = pos=(66.5,39,2) rot=(0,0,1;0rad)
  Radius = 3.75
  SecondAngle = 0
FEATURE [Part::Cylinder] Cylinder014
  Angle = 360
  AttacherType = Attacher::AttachEngine3D
  FirstAngle = 0
  Height = 3.15
  Placement = pos=(7.5,39,2) rot=(0,0,1;0rad)
  Radius = 3.75
  SecondAngle = 0
FEATURE [Part::Cylinder] Cylinder015
  Angle = 360
  AttacherType = Attacher::AttachEngine3D
  FirstAngle = 0
  Height = 3.15
  Placement = pos=(66.5,75.5,2) rot=(0,0,1;0rad)
  Radius = 3.75
  SecondAngle = 0
FEATURE [Part::MultiFuse] Fusion007  label="m4headBottomCut"
  Placement = pos=(0,0,-2) rot=(0,0,1;0rad)
  Shapes = -> [Cylinder015,Cylinder012,Cylinder013,Cylinder014]
FEATURE [Sketcher::SketchObject] Sketch004
  FullyConstrained = true
  Placement = pos=(0,0,0) rot=(1,0,0;1.5708rad)
  sketch-geometry (46):
    g0: LineSegment StartX=11.75 StartY=19.5 StartZ=0 EndX=21.5 EndY=19.5 EndZ=0
    g1: LineSegment StartX=21.5 StartY=19.5 StartZ=0 EndX=23.75 EndY=22 EndZ=0
    g2: LineSegment StartX=23.75 StartY=22 StartZ=0 EndX=23.75 EndY=25 EndZ=0
    g3: LineSegment StartX=23.75 StartY=25 StartZ=0 EndX=9.5 EndY=25 EndZ=0
    g4: LineSegment StartX=9.5 StartY=25 StartZ=0 EndX=9.5 EndY=22 EndZ=0
    g5: LineSegment StartX=40 StartY=24.5 StartZ=0 EndX=40 EndY=22 EndZ=0
    g6: LineSegment StartX=40 StartY=22 StartZ=0 EndX=42.5 EndY=19.5 EndZ=0
    g7: LineSegment StartX=42.5 StartY=19.5 StartZ=0 EndX=48.7 EndY=19.5 EndZ=0
    g8: LineSegment StartX=48.7 StartY=19.5 StartZ=0 EndX=51.2 EndY=22 EndZ=0
    g9: LineSegment StartX=51.2 StartY=22 StartZ=0 EndX=51.2 EndY=24.5 EndZ=0
    g10: LineSegment StartX=51.2 StartY=24.5 StartZ=0 EndX=40 EndY=24.5 EndZ=0
    g11: LineSegment StartX=52.45 StartY=24.5 StartZ=0 EndX=52.45 EndY=22 EndZ=0
    g12: LineSegment StartX=52.45 StartY=22 StartZ=0 EndX=54.95 EndY=19.5 EndZ=0
    g13: LineSegment StartX=54.95 StartY=19.5 StartZ=0 EndX=61.15 EndY=19.5 EndZ=0
    g14: LineSegment StartX=61.15 StartY=19.5 StartZ=0 EndX=63.65 EndY=22 EndZ=0
    g15: LineSegment StartX=63.65 StartY=22 StartZ=0 EndX=63.65 EndY=24.5 EndZ=0
    g16: LineSegment StartX=63.65 StartY=24.5 StartZ=0 EndX=52.45 EndY=24.5 EndZ=0
    g17: LineSegment StartX=9.5 StartY=22 StartZ=0 EndX=11.75 EndY=19.5 EndZ=0
    g18: ArcOfCircle CenterX=12.3 CenterY=15.45 CenterZ=0 NormalX=0 NormalY=0 NormalZ=1 AngleXU=0 Radius=1 StartAngle=1.5708 EndAngle=3.14159
    g19: LineSegment StartX=11.3 StartY=15.45 StartZ=0 EndX=11.3 EndY=14.2 EndZ=0
    g20: LineSegment StartX=12.3 StartY=16.45 StartZ=0 EndX=16.8 EndY=16.45 EndZ=0
    g21: ArcOfCircle CenterX=16.8 CenterY=15.45 CenterZ=0 NormalX=0 NormalY=0 NormalZ=1 AngleXU=0 Radius=1 StartAngle=3e-16 EndAngle=1.5708
    g22: ArcOfCircle CenterX=16.8 CenterY=14.2 CenterZ=0 NormalX=0 NormalY=0 NormalZ=1 AngleXU=0 Radius=1 StartAngle=4.71239 EndAngle=6.28319
    g23: ArcOfCircle CenterX=12.3 CenterY=14.2 CenterZ=0 NormalX=0 NormalY=0 NormalZ=1 AngleXU=0 Radius=1 StartAngle=3.14159 EndAngle=4.71239
    g24: LineSegment StartX=12.3 StartY=13.2 StartZ=0 EndX=16.8 EndY=13.2 EndZ=0
    g25: LineSegment StartX=17.8 StartY=15.45 StartZ=0 EndX=17.8 EndY=14.2 EndZ=0
    g26: Circle CenterX=18.9 CenterY=16.475 CenterZ=0 NormalX=0 NormalY=0 NormalZ=1 AngleXU=0 Radius=0.5
    g27: Circle CenterX=21.09 CenterY=16.475 CenterZ=0 NormalX=0 NormalY=0 NormalZ=1 AngleXU=0 Radius=0.5
    g28: Circle CenterX=23.28 CenterY=16.475 CenterZ=0 NormalX=0 NormalY=0 NormalZ=1 AngleXU=0 Radius=0.5
    g29: Circle CenterX=25.47 CenterY=16.475 CenterZ=0 NormalX=0 NormalY=0 NormalZ=1 AngleXU=0 Radius=0.5
    g30: LineSegment StartX=44.8 StartY=16.45 StartZ=0 EndX=49.3 EndY=16.45 EndZ=0
    g31: LineSegment StartX=50.3 StartY=15.45 StartZ=0 EndX=50.3 EndY=14.2 EndZ=0
    g32: LineSegment StartX=49.3 StartY=13.2 StartZ=0 EndX=44.8 EndY=13.2 EndZ=0
    g33: LineSegment StartX=43.8 StartY=15.45 StartZ=0 EndX=43.8 EndY=14.2 EndZ=0
    g34: ArcOfCircle CenterX=44.8 CenterY=15.45 CenterZ=0 NormalX=0 NormalY=0 NormalZ=1 AngleXU=0 Radius=1 StartAngle=1.5708 EndAngle=3.14159
    g35: ArcOfCircle CenterX=49.3 CenterY=15.45 CenterZ=0 NormalX=0 NormalY=0 NormalZ=1 AngleXU=0 Radius=1 StartAngle=3e-16 EndAngle=1.5708
    g36: ArcOfCircle CenterX=49.3 CenterY=14.2 CenterZ=0 NormalX=0 NormalY=0 NormalZ=1 AngleXU=0 Radius=1 StartAngle=4.71239 EndAngle=6.28319
    g37: ArcOfCircle CenterX=44.8 CenterY=14.2 CenterZ=0 NormalX=0 NormalY=0 NormalZ=1 AngleXU=0 Radius=1 StartAngle=3.14159 EndAngle=4.71239
    g38: LineSegment StartX=52.25 StartY=15.58 StartZ=0 EndX=52.25 EndY=14.58 EndZ=0
    g39: LineSegment StartX=53.5 StartY=16.83 StartZ=0 EndX=60.5 EndY=16.83 EndZ=0
    g40: LineSegment StartX=53.5 StartY=13.33 StartZ=0 EndX=60.5 EndY=13.33 EndZ=0
    g41: LineSegment StartX=61.75 StartY=15.58 StartZ=0 EndX=61.75 EndY=14.58 EndZ=0
    g42: ArcOfCircle CenterX=53.5 CenterY=15.58 CenterZ=0 NormalX=0 NormalY=0 NormalZ=1 AngleXU=0 Radius=1.25 StartAngle=1.5708 EndAngle=3.14159
    g43: ArcOfCircle CenterX=60.5 CenterY=15.58 CenterZ=0 NormalX=0 NormalY=0 NormalZ=1 AngleXU=0 Radius=1.25 StartAngle=2e-16 EndAngle=1.5708
    g44: ArcOfCircle CenterX=60.5 CenterY=14.58 CenterZ=0 NormalX=0 NormalY=0 NormalZ=1 AngleXU=0 Radius=1.25 StartAngle=4.7124 EndAngle=6.28319
    g45: ArcOfCircle CenterX=53.5 CenterY=14.58 CenterZ=0 NormalX=0 NormalY=0 NormalZ=1 AngleXU=0 Radius=1.25 StartAngle=3.14159 EndAngle=4.71239
  constraints (150):
    c: Horizontal(g0)
    c: Coincident(g0,g1)
    c: Coincident(g1,g2)
    c: Coincident(g2,g3)
    c: Horizontal(g3)
    c: Coincident(g3,g4)
    c: Vertical(g4)
    c: Coincident(g5,g6)
    c: Coincident(g6,g7)
    c: Horizontal(g7)
    c: Coincident(g7,g8)
    c: Coincident(g8,g9)
    c: Vertical(g9)
    c: Coincident(g9,g10)
    c: Coincident(g10,g5)
    c: Coincident(g11,g12)
    c: Coincident(g12,g13)
    c: Horizontal(g13)
    c: Coincident(g13,g14)
    c: Coincident(g14,g15)
    c: Vertical(g15)
    c: Coincident(g15,g16)
    c: Coincident(g16,g11)
    c: Horizontal(g16)
    c: Coincident(g17,g4)
    c: Coincident(g0,g17)
    c: DistanceX(g3) = 9.5
    c: DistanceX(g3,g3) = 14.25
    c: Vertical(g2)
    c: DistanceY(g3) = 25
    c: DistanceY(g4) = 22
    c: DistanceY(g4,g1) = 0
    c: DistanceX(g4,g0) = 2.25
    c: DistanceX(g0,g1) = 2.25
    c: Horizontal(g10)
    c: Vertical(g5)
    c: Vertical(g11)
    c: DistanceX(g5) = 40
    c: DistanceX(g5,g9) = 11.2
    c: DistanceY(g11,g9) = 0
    c: DistanceY(g5,g5) = 2.5
    c: DistanceY(g8,g5) = 0
    c: DistanceY(g11,g8) = 0
    c: DistanceY(g14,g11) = 0
    c: DistanceY(g6,g5) = 2.5
    c: DistanceX(g5,g6) = 2.5
    c: DistanceX(g7,g8) = 2.5
    c: DistanceX(g9,g11) = 1.25
    c: DistanceY(g12,g7) = 0
    c: DistanceX(g11,g12) = 2.5
    c: DistanceX(g13,g14) = 2.5
    c: DistanceX(g11,g15) = 11.2
    c: DistanceY(g0,g4) = 2.5
    c: DistanceY(g5) = 24.5
    c: Coincident(g19,g18)
    c: Vertical(g19)
    c: Horizontal(g20)
    c: Coincident(g21,g20)
    c: Coincident(g23,g19)
    c: Coincident(g24,g23)
    c: Coincident(g24,g22)
    c: Horizontal(g24)
    c: Coincident(g25,g21)
    c: Coincident(g25,g22)
    c: Vertical(g25)
    c: Coincident(g18,g20)
    c: Radius(g18) = 1
    c: Angle(g18) = 1.5708
    c: Angle(g21) = 1.5708
    c: Angle(g22) = 1.5708
    c: Angle(g23) = 1.5708
    c: DistanceX(g23) = 12.3
    c: DistanceY(g23) = 13.2
    c: DistanceX(g19) = 11.3
    c: DistanceY(g23,g19) = 0
    c: DistanceY(g18,g18) = 0
    c: DistanceX(g21,g20) = 0
    c: Radius(g21) = 1
    c: Radius(g22) = 1
    c: DistanceX(g22,g22) = 0
    c: DistanceX(g18,g20) = 4.5
    c: DistanceX(g26) = 18.9
    c: Radius(g26) = 0.5
    c: DistanceY(g26) = 16.475
    c: DistanceX(g26,g27) = 2.19
    c: DistanceY(g26,g27) = 0
    c: DistanceY(g28,g27) = 0
    c: DistanceY(g29,g28) = 0
    c: DistanceX(g27,g28) = 2.19
    c: Radius(g27) = 0.5
    c: Radius(g28) = 0.5
    c: Radius(g29) = 0.5
    c: DistanceX(g28,g29) = 2.19
    c: DistanceY(g23,g18) = 1.25
    c: Horizontal(g30)
    c: Vertical(g31)
    c: Vertical(g33)
    c: Coincident(g33,g34)
    c: Coincident(g33,g37)
    c: Coincident(g32,g37)
    c: Coincident(g32,g36)
    c: Coincident(g31,g36)
    c: Coincident(g31,g35)
    c: Coincident(g30,g35)
    c: Coincident(g30,g34)
    c: Angle(g34) = 1.5708
    c: Angle(g35) = 1.5708
    c: Angle(g37) = 1.5708
    c: Angle(g36) = 1.5708
    c: DistanceY(g18,g34) = 0
    c: DistanceY(g34,g33) = 0
    c: Radius(g34) = 1
    c: DistanceY(g33,g37) = 0
    c: Radius(g37) = 1
    c: Radius(g36) = 1
    c: Radius(g35) = 1
    c: DistanceY(g33,g23) = 0
    c: DistanceY(g31,g36) = 0
    c: Horizontal(g32)
    c: DistanceX(g35,g30) = 0
    c: DistanceX(g32,g32) = 4.5
    c: Vertical(g38)
    c: Horizontal(g39)
    c: Horizontal(g40)
    c: Vertical(g41)
    c: Coincident(g42,g38)
    c: Coincident(g42,g39)
    c: Coincident(g43,g39)
    c: Coincident(g45,g38)
    c: Coincident(g45,g40)
    c: Coincident(g40,g44)
    c: Coincident(g41,g44)
    c: Coincident(g41,g43)
    c: DistanceX(g42) = 53.5
    c: DistanceY(g42) = 15.58
    c: DistanceX(g42,g45) = 0
    c: DistanceY(g45,g42) = 1
    c: Radius(g42) = 1.25
    c: Radius(g44) = 1.25
    c: Radius(g43) = 1.25
    c: DistanceX(g45,g40) = 0
    c: DistanceX(g42,g39) = 0
    c: DistanceY(g42,g43) = 0
    c: DistanceY(g44,g45) = 0
    c: DistanceY(g45,g38) = 0
    c: DistanceX(g42,g43) = 7
    c: DistanceX(g18,g34) = 32.5
    c: DistanceY(g41,g44) = 0
    c: DistanceY(g43,g41) = 0
    c: Angle(g42) = 1.5708
FEATURE [Part::Extrusion] Extrude004  label="lightBottomCutDone"
  Base = -> Sketch004
  Dir = (0,-1,2e-16)
  DirMode = 2
  FaceMakerClass = Part::FaceMakerBullseye
  LengthFwd = 2
  LengthRev = 0
  Placement = pos=(0,2,0) rot=(0,0,1;0rad)
  Solid = true
  Symmetric = false
FEATURE [Sketcher::SketchObject] Sketch007
  FullyConstrained = true
  sketch-geometry (48):
    g0: LineSegment StartX=4 StartY=77 StartZ=0 EndX=6 EndY=77 EndZ=0
    g1: LineSegment StartX=6 StartY=77 StartZ=0 EndX=-3.99999 EndY=59.6795 EndZ=0
    g2: LineSegment StartX=-3.99999 StartY=59.6795 StartZ=0 EndX=-5.99999 EndY=59.6795 EndZ=0
    g3: LineSegment StartX=-5.99999 StartY=59.6795 StartZ=0 EndX=4 EndY=77 EndZ=0
    g4: LineSegment StartX=-5.99999 StartY=52.6795 StartZ=0 EndX=-3.99999 EndY=52.6795 EndZ=0
    g5: LineSegment StartX=-5.99999 StartY=52.6795 StartZ=0 EndX=4 EndY=70 EndZ=0
    g6: LineSegment StartX=4 StartY=70 StartZ=0 EndX=6 EndY=70 EndZ=0
    g7: LineSegment StartX=6 StartY=70 StartZ=0 EndX=-3.99999 EndY=52.6795 EndZ=0
    g8: LineSegment StartX=-3.99999 StartY=45.6795 StartZ=0 EndX=-5.99999 EndY=45.6795 EndZ=0
    g9: LineSegment StartX=-5.99999 StartY=45.6795 StartZ=0 EndX=4 EndY=63 EndZ=0
    g10: LineSegment StartX=4 StartY=63 StartZ=0 EndX=6 EndY=63 EndZ=0
    g11: LineSegment StartX=6 StartY=63 StartZ=0 EndX=-3.99999 EndY=45.6795 EndZ=0
    g12: LineSegment StartX=4 StartY=56 StartZ=0 EndX=6 EndY=56 EndZ=0
    g13: LineSegment StartX=6 StartY=56 StartZ=0 EndX=-3.99999 EndY=38.6795 EndZ=0
    g14: LineSegment StartX=-3.99999 StartY=38.6795 StartZ=0 EndX=-5.99999 EndY=38.6795 EndZ=0
    g15: LineSegment StartX=-5.99999 StartY=38.6795 StartZ=0 EndX=4 EndY=56 EndZ=0
    g16: LineSegment StartX=4 StartY=49 StartZ=0 EndX=6 EndY=49 EndZ=0
    g17: LineSegment StartX=6 StartY=49 StartZ=0 EndX=-3.99999 EndY=31.6795 EndZ=0
    g18: LineSegment StartX=-3.99999 StartY=31.6795 StartZ=0 EndX=-5.99999 EndY=31.6795 EndZ=0
    g19: LineSegment StartX=-5.99999 StartY=31.6795 StartZ=0 EndX=4 EndY=49 EndZ=0
    g20: LineSegment StartX=4 StartY=42 StartZ=0 EndX=6 EndY=42 EndZ=0
    g21: LineSegment StartX=6 StartY=42 StartZ=0 EndX=-3.99999 EndY=24.6795 EndZ=0
    g22: LineSegment StartX=-3.99999 StartY=24.6795 StartZ=0 EndX=-5.99999 EndY=24.6795 EndZ=0
    g23: LineSegment StartX=-5.99999 StartY=24.6795 StartZ=0 EndX=4 EndY=42 EndZ=0
    g24: LineSegment StartX=70 StartY=77 StartZ=0 EndX=68 EndY=77 EndZ=0
    g25: LineSegment StartX=68 StartY=77 StartZ=0 EndX=78 EndY=59.6795 EndZ=0
    g26: LineSegment StartX=78 StartY=59.6795 StartZ=0 EndX=80 EndY=59.6795 EndZ=0
    g27: LineSegment StartX=80 StartY=59.6795 StartZ=0 EndX=70 EndY=77 EndZ=0
    g28: LineSegment StartX=68 StartY=70 StartZ=0 EndX=70 EndY=70 EndZ=0
    g29: LineSegment StartX=70 StartY=70 StartZ=0 EndX=80 EndY=52.6795 EndZ=0
    g30: LineSegment StartX=80 StartY=52.6795 StartZ=0 EndX=78 EndY=52.6795 EndZ=0
    g31: LineSegment StartX=78 StartY=52.6795 StartZ=0 EndX=68 EndY=70 EndZ=0
    g32: LineSegment StartX=68 StartY=63 StartZ=0 EndX=70 EndY=63 EndZ=0
    g33: LineSegment StartX=70 StartY=63 StartZ=0 EndX=80 EndY=45.6795 EndZ=0
    g34: LineSegment StartX=80 StartY=45.6795 StartZ=0 EndX=78 EndY=45.6795 EndZ=0
    g35: LineSegment StartX=78 StartY=45.6795 StartZ=0 EndX=68 EndY=63 EndZ=0
    g36: LineSegment StartX=68 StartY=56 StartZ=0 EndX=70 EndY=56 EndZ=0
    g37: LineSegment StartX=70 StartY=56 StartZ=0 EndX=80 EndY=38.6795 EndZ=0
    g38: LineSegment StartX=80 StartY=38.6795 StartZ=0 EndX=78 EndY=38.6795 EndZ=0
    g39: LineSegment StartX=78 StartY=38.6795 StartZ=0 EndX=68 EndY=56 EndZ=0
    g40: LineSegment StartX=68 StartY=49 StartZ=0 EndX=70 EndY=49 EndZ=0
    g41: LineSegment StartX=70 StartY=49 StartZ=0 EndX=80 EndY=31.6795 EndZ=0
    g42: LineSegment StartX=80 StartY=31.6795 StartZ=0 EndX=78 EndY=31.6795 EndZ=0
    g43: LineSegment StartX=78 StartY=31.6795 StartZ=0 EndX=68 EndY=49 EndZ=0
    g44: LineSegment StartX=68 StartY=42 StartZ=0 EndX=70 EndY=42 EndZ=0
    g45: LineSegment StartX=70 StartY=42 StartZ=0 EndX=80 EndY=24.6795 EndZ=0
    g46: LineSegment StartX=80 StartY=24.6795 StartZ=0 EndX=78 EndY=24.6795 EndZ=0
    g47: LineSegment StartX=78 StartY=24.6795 StartZ=0 EndX=68 EndY=42 EndZ=0
  constraints (144):
    c: Coincident(g3,g0)
    c: DistanceX(g2,g2) = 2
    c: DistanceX(g0,g0) = 2
    c: Angle(g1) = -2.0944
    c: Distance(g3) = 20
    c: Coincident(g2,g3)
    c: DistanceX(g0) = 4
    c: DistanceY(g0) = 77
    c: Coincident(g4,g5)
    c: Coincident(g6,g7)
    c: Coincident(g7,g4)
    c: Horizontal(g6)
    c: DistanceX(g5,g0) = 0
    c: DistanceY(g5,g0) = 7
    c: DistanceX(g2,g4) = 0
    c: DistanceX(g1,g4) = 0
    c: DistanceY(g4,g2) = 7
    c: Horizontal(g4)
    c: Angle(g5) = 1.0472
    c: Horizontal(g8)
    c: Coincident(g9,g8)
    c: Horizontal(g10)
    c: Coincident(g11,g8)
    c: Coincident(g9,g10)
    c: Coincident(g10,g11)
    c: DistanceX(g5,g9) = 0
    c: DistanceX(g10,g6) = 0
    c: DistanceY(g9,g5) = 7
    c: DistanceY(g8,g4) = 7
    c: DistanceX(g8,g4) = 0
    c: DistanceX(g4,g8) = 0
    c: Horizontal(g12)
    c: Coincident(g13,g12)
    c: Horizontal(g14)
    c: Coincident(g15,g12)
    c: Coincident(g1,g2)
    c: Horizontal(g2)
    c: DistanceX(g12,g12) = 2
    c: DistanceX(g9,g12) = 0
    c: DistanceY(g12,g9) = 7
    c: DistanceY(g14,g8) = 7
    c: Coincident(g14,g13)
    c: Coincident(g14,g15)
    c: DistanceX(g14,g8) = 0
    c: DistanceX(g8,g13) = 0
    c: Horizontal(g16)
    c: Coincident(g17,g16)
    c: Horizontal(g18)
    c: Coincident(g19,g16)
    c: DistanceX(g16,g16) = 2
    c: DistanceY(g16,g12) = 7
    c: DistanceX(g12,g16) = 0
    c: DistanceX(g18,g14) = 0
    c: Coincident(g18,g19)
    c: Coincident(g17,g18)
    c: DistanceY(g18,g14) = 7
    c: DistanceX(g18,g18) = 2
    c: Horizontal(g20)
    c: Coincident(g20,g21)
    c: Coincident(g21,g22)
    c: Coincident(g22,g23)
    c: Coincident(g23,g20)
    c: DistanceX(g16,g20) = 0
    c: DistanceY(g20,g16) = 7
    c: DistanceY(g22,g18) = 7
    c: DistanceX(g22,g18) = 0
    c: Horizontal(g22)
    c: DistanceX(g22,g22) = 2
    c: DistanceX(g20,g20) = 2
    c: Horizontal(g24)
    c: Coincident(g25,g24)
    c: Coincident(g26,g25)
    c: Horizontal(g26)
    c: Coincident(g27,g24)
    c: DistanceX(g24,g24) = 2
    c: DistanceX(g0,g24) = 66
    c: DistanceY(g24,g0) = 0
    c: Distance(g25) = 20
    c: Coincident(g26,g27)
    c: Angle(g27) = 2.0944
    c: DistanceX(g26,g26) = 2
    c: Horizontal(g28)
    c: Coincident(g29,g28)
    c: Coincident(g30,g29)
    c: Coincident(g31,g28)
    c: Coincident(g33,g32)
    c: Coincident(g34,g33)
    c: Coincident(g35,g32)
    c: Coincident(g37,g36)
    c: Coincident(g38,g37)
    c: Coincident(g39,g36)
    c: DistanceY(g28,g6) = 0
    c: DistanceY(g32,g9) = 0
    c: DistanceY(g36,g12) = 0
    c: DistanceX(g24,g28) = 0
    c: DistanceX(g32,g28) = 0
    c: DistanceX(g36,g32) = 0
    c: Horizontal(g36)
    c: Horizontal(g32)
    c: DistanceX(g32,g32) = 2
    c: DistanceX(g36,g36) = 2
    c: Horizontal(g30)
    c: Horizontal(g34)
    c: Horizontal(g38)
    c: Coincident(g34,g35)
    c: Coincident(g30,g31)
    c: DistanceX(g25,g30) = 0
    c: DistanceX(g30,g34) = 0
    c: DistanceX(g34,g34) = 2
    c: DistanceX(g30,g30) = 2
    c: Coincident(g38,g39)
    c: DistanceX(g38,g38) = 2
    c: DistanceX(g34,g38) = 0
    c: Horizontal(g40)
    c: Coincident(g41,g40)
    c: Horizontal(g42)
    c: Coincident(g43,g40)
    c: DistanceY(g40,g16) = 0
    c: Horizontal(g44)
    c: Coincident(g45,g44)
    c: Coincident(g46,g45)
    c: Horizontal(g46)
    c: Coincident(g47,g44)
    c: DistanceY(g20,g44) = 0
    c: DistanceX(g44,g40) = 0
    c: DistanceX(g40,g36) = 0
    c: DistanceX(g44,g44) = 2
    c: DistanceX(g40,g40) = 2
    c: DistanceX(g46,g46) = 2
    c: DistanceX(g42,g42) = 2
    c: Coincident(g42,g43)
    c: Coincident(g41,g42)
    c: Coincident(g46,g47)
    c: DistanceX(g42,g38) = 0
    c: DistanceX(g46,g42) = 0
    c: DistanceY(g46,g42) = 7
    c: DistanceY(g42,g38) = 7
    c: DistanceY(g38,g34) = 7
    c: DistanceY(g34,g30) = 7
    c: DistanceY(g30,g25) = 7
    c: DistanceX(g28,g28) = 2
    c: Coincident(g0,g1)
    c: DistanceX(g6,g6) = 2
    c: Coincident(g5,g6)
FEATURE [Part::Extrusion] Extrude007  label="ventsBottomCut"
  Base = -> Sketch007
  Dir = (0,0,1)
  DirMode = 2
  FaceMakerClass = Part::FaceMakerBullseye
  LengthFwd = 20
  LengthRev = 0
  Placement = pos=(0,0,5) rot=(0,0,1;0rad)
  Solid = true
  Symmetric = false
FEATURE [Part::Cylinder] Cylinder016
  Angle = 360
  AttacherType = Attacher::AttachEngine3D
  FirstAngle = 0
  Height = 14
  Placement = pos=(7.5,75.5,2) rot=(0,0,1;0rad)
  Radius = 2
  SecondAngle = 0
FEATURE [Part::Cylinder] Cylinder017
  Angle = 360
  AttacherType = Attacher::AttachEngine3D
  FirstAngle = 0
  Height = 14
  Placement = pos=(66.5,39,2) rot=(0,0,1;0rad)
  Radius = 2
  SecondAngle = 0
FEATURE [Part::Cylinder] Cylinder018
  Angle = 360
  AttacherType = Attacher::AttachEngine3D
  FirstAngle = 0
  Height = 14
  Placement = pos=(7.5,39,2) rot=(0,0,1;0rad)
  Radius = 2
  SecondAngle = 0
FEATURE [Part::Cylinder] Cylinder019
  Angle = 360
  AttacherType = Attacher::AttachEngine3D
  FirstAngle = 0
  Height = 14
  Placement = pos=(66.5,75.5,2) rot=(0,0,1;0rad)
  Radius = 2
  SecondAngle = 0
FEATURE [Part::MultiFuse] Fusion009  label="basesM3TopCut"
  Placement = pos=(0,0,12.25) rot=(0,0,1;0rad)
  Shapes = -> [Cylinder019,Cylinder016,Cylinder017,Cylinder018]
FEATURE [Sketcher::SketchObject] Sketch008
  FullyConstrained = true
  MapMode = 2
  Placement = pos=(0,0,12.25) rot=(0,0,1;0rad)
  Support = -> [Fusion009]
  sketch-geometry (10):
    g0: LineSegment StartX=2.5 StartY=80.5 StartZ=0 EndX=2.5 EndY=2.5 EndZ=0
    g1: LineSegment StartX=2.5 StartY=2.5 StartZ=0 EndX=36 EndY=2.5 EndZ=0
    g2: LineSegment StartX=71.5 StartY=23.25 StartZ=0 EndX=71.5 EndY=80.5 EndZ=0
    g3: LineSegment StartX=2.5 StartY=80.5 StartZ=0 EndX=71.5 EndY=80.5 EndZ=0
    g4: LineSegment StartX=36 StartY=2.5 StartZ=0 EndX=36 EndY=3.5 EndZ=0
    g5: LineSegment StartX=36 StartY=3.5 StartZ=0 EndX=3.5 EndY=3.5 EndZ=0
    g6: LineSegment StartX=3.5 StartY=3.5 StartZ=0 EndX=3.5 EndY=79.5 EndZ=0
    g7: LineSegment StartX=3.5 StartY=79.5 StartZ=0 EndX=70.5 EndY=79.5 EndZ=0
    g8: LineSegment StartX=70.5 StartY=79.5 StartZ=0 EndX=70.5 EndY=23.25 EndZ=0
    g9: LineSegment StartX=70.5 StartY=23.25 StartZ=0 EndX=71.5 EndY=23.25 EndZ=0
  constraints (30):
    c: Vertical(g0)
    c: Horizontal(g1)
    c: Vertical(g2)
    c: Coincident(g3,g2)
    c: DistanceX(g-1,g0) = 2.5
    c: DistanceY(g0) = 2.5
    c: Coincident(g1,g0)
    c: Coincident(g0,g3)
    c: Coincident(g4,g1)
    c: Vertical(g4)
    c: Horizontal(g5)
    c: Coincident(g6,g5)
    c: Vertical(g6)
    c: Horizontal(g7)
    c: Coincident(g8,g7)
    c: Vertical(g8)
    c: Coincident(g9,g8)
    c: Coincident(g9,g2)
    c: DistanceX(g5) = 3.5
    c: DistanceY(g-1,g5) = 3.5
    c: DistanceX(g0,g1) = 33.5
    c: Coincident(g5,g4)
    c: Coincident(g6,g7)
    c: DistanceY(g0,g0) = 78
    c: DistanceY(g6,g0) = 1
    c: DistanceX(g7,g2) = 1
    c: DistanceX(g0,g2) = 69
    c: Horizontal(g9)
    c: DistanceY(g8,g7) = 56.25
    c: Horizontal(g3)
FEATURE [Part::Extrusion] Extrude008  label="topAlineIn"
  Base = -> Sketch008
  Dir = (0,0,1)
  DirMode = 2
  FaceMakerClass = Part::FaceMakerBullseye
  LengthFwd = 1.5
  LengthRev = 0
  Placement = pos=(0,0,15) rot=(0,0,1;0rad)
  Solid = true
  Symmetric = false
FEATURE [Part::Cut] Cut002  label="bottom004Done"
  Base = -> Cut
  Tool = -> Extrude007
FEATURE [Sketcher::SketchObject] Sketch009
  FullyConstrained = true
  MapMode = 4
  Placement = pos=(0,0,0) rot=(0.57735,0.57735,0.57735;2.0944rad)
  sketch-geometry (1):
    g0: Circle CenterX=79 CenterY=2 CenterZ=0 NormalX=0 NormalY=0 NormalZ=1 AngleXU=0 Radius=2
  constraints (3):
    c: DistanceX(g0) = 79
    c: DistanceY(g0) = 2
    c: Radius(g0) = 2
FEATURE [Part::Extrusion] Extrude009  label="bottomInTagHoldInDone"
  Base = -> Sketch009
  Dir = (1,0,0)
  DirMode = 2
  FaceMakerClass = Part::FaceMakerBullseye
  LengthFwd = 70
  LengthRev = 0
  Placement = pos=(2,2,0) rot=(0,0,1;0rad)
  Solid = true
  Symmetric = false
FEATURE [Sketcher::SketchObject] Sketch011
  FullyConstrained = true
  Placement = pos=(0,0,0) rot=(0.57735,0.57735,0.57735;2.0944rad)
  sketch-geometry (2):
    g0: Circle CenterX=79 CenterY=2 CenterZ=0 NormalX=0 NormalY=0 NormalZ=1 AngleXU=0 Radius=3.5
    g1: Circle CenterX=79 CenterY=2 CenterZ=0 NormalX=0 NormalY=0 NormalZ=1 AngleXU=0 Radius=2
  constraints (5):
    c: Radius(g0) = 3.5
    c: Radius(g1) = 2
    c: Coincident(g0,g1)
    c: DistanceX(g0) = 79
    c: DistanceY(g0) = 2
FEATURE [Part::Extrusion] Extrude011  label="tagBottomCutDone"
  Base = -> Sketch011
  Dir = (1,0,0)
  DirMode = 2
  FaceMakerClass = Part::FaceMakerBullseye
  LengthFwd = 10
  LengthRev = 0
  Placement = pos=(32,2,0) rot=(0,0,1;0rad)
  Solid = true
  Symmetric = false
FEATURE [Part::MultiFuse] Fusion012  label="bottomIn"
  Shapes = -> [Extrude009,Cut002,Fillet004,Fillet003,Fusion]
FEATURE [Part::MultiFuse] Fusion014  label="topBasesIn"
  Placement = pos=(0,0,18.25) rot=(0,0,1;0rad)
  Shapes = -> [Cylinder008,Cylinder009,Cylinder010,Cylinder011]
FEATURE [Part::MultiFuse] Fusion015  label="topIn"
  Placement = pos=(0,0,1) rot=(0,0,1;0rad)
  Shapes = -> [Fusion014,Extrude008,Fillet005]
FEATURE [Sketcher::SketchObject] Sketch012
  FullyConstrained = true
  Placement = pos=(0,0,0) rot=(0.57735,0.57735,0.57735;2.0944rad)
  sketch-geometry (4):
    g0: LineSegment StartX=8 StartY=23 StartZ=0 EndX=26 EndY=23 EndZ=0
    g1: LineSegment StartX=26 StartY=23 StartZ=0 EndX=26 EndY=20 EndZ=0
    g2: LineSegment StartX=26 StartY=20 StartZ=0 EndX=8 EndY=20 EndZ=0
    g3: LineSegment StartX=8 StartY=20 StartZ=0 EndX=8 EndY=23 EndZ=0
  constraints (12):
    c: Coincident(g0,g1)
    c: Coincident(g1,g2)
    c: Coincident(g2,g3)
    c: Coincident(g3,g0)
    c: Horizontal(g0)
    c: Horizontal(g2)
    c: Vertical(g1)
    c: Vertical(g3)
    c: DistanceX(g2) = 8
    c: DistanceX(g2,g0) = 18
    c: DistanceY(g2) = 20
    c: DistanceY(g2,g0) = 3
FEATURE [Part::Extrusion] Extrude012  label="leftInCut"
  Base = -> Sketch012
  Dir = (1,0,0)
  DirMode = 2
  FaceMakerClass = Part::FaceMakerBullseye
  LengthFwd = 2
  LengthRev = 0
  Placement = pos=(72,1,0) rot=(0,0,1;0rad)
  Solid = true
  Symmetric = false
FEATURE [Sketcher::SketchObject] Sketch013
  FullyConstrained = true
  MapMode = 4
  Placement = pos=(72,1,0) rot=(0.57735,0.57735,0.57735;2.0944rad)
  Support = -> [Extrude012]
  sketch-geometry (4):
    g0: LineSegment StartX=26 StartY=19.9 StartZ=0 EndX=12 EndY=19.9 EndZ=0
    g1: LineSegment StartX=12 StartY=19.9 StartZ=0 EndX=12 EndY=22.9 EndZ=0
    g2: LineSegment StartX=12 StartY=22.9 StartZ=0 EndX=26 EndY=22.9 EndZ=0
    g3: LineSegment StartX=26 StartY=22.9 StartZ=0 EndX=26 EndY=19.9 EndZ=0
  constraints (12):
    c: Coincident(g0,g1)
    c: Coincident(g1,g2)
    c: Coincident(g2,g3)
    c: Coincident(g3,g0)
    c: Horizontal(g0)
    c: Horizontal(g2)
    c: Vertical(g1)
    c: Vertical(g3)
    c: DistanceX(g0,g0) = 14
    c: DistanceX(g1) = 12
    c: DistanceY(g1) = 22.9
    c: DistanceY(g1,g1) = 3
FEATURE [Part::Extrusion] Extrude013  label="sdCut"
  Base = -> Sketch013
  Dir = (1,0,0)
  DirMode = 2
  FaceMakerClass = Part::FaceMakerBullseye
  LengthFwd = 2
  LengthRev = 0
  Placement = pos=(-72,0,0) rot=(0,0,1;0rad)
  Solid = true
  Symmetric = false
FEATURE [Part::MultiFuse] Fusion017  label="bottomCutsHorDone"
  Shapes = -> [Extrude013,Extrude012]
FEATURE [Sketcher::SketchObject] Sketch014
  FullyConstrained = true
  Placement = pos=(0,0,0) rot=(1,0,0;1.5708rad)
  sketch-geometry (8):
    g0: ArcOfCircle CenterX=12.75 CenterY=15.23 CenterZ=0 NormalX=0 NormalY=0 NormalZ=1 AngleXU=0 Radius=0.9 StartAngle=1.5708 EndAngle=3.14159
    g1: ArcOfCircle CenterX=16.35 CenterY=15.23 CenterZ=0 NormalX=0 NormalY=0 NormalZ=1 AngleXU=0 Radius=0.9 StartAngle=8e-16 EndAngle=1.5708
    g2: ArcOfCircle CenterX=16.35 CenterY=14.43 CenterZ=0 NormalX=0 NormalY=0 NormalZ=1 AngleXU=0 Radius=0.9 StartAngle=4.71239 EndAngle=6.28319
    g3: ArcOfCircle CenterX=12.75 CenterY=14.43 CenterZ=0 NormalX=0 NormalY=0 NormalZ=1 AngleXU=0 Radius=0.9 StartAngle=3.14159 EndAngle=4.71239
    g4: LineSegment StartX=12.75 StartY=16.13 StartZ=0 EndX=16.35 EndY=16.13 EndZ=0
    g5: LineSegment StartX=17.25 StartY=15.23 StartZ=0 EndX=17.25 EndY=14.43 EndZ=0
    g6: LineSegment StartX=16.35 StartY=13.53 StartZ=0 EndX=12.75 EndY=13.53 EndZ=0
    g7: LineSegment StartX=11.85 StartY=14.43 StartZ=0 EndX=11.85 EndY=15.23 EndZ=0
  constraints (28):
    c: Coincident(g4,g0)
    c: Coincident(g4,g1)
    c: Horizontal(g4)
    c: Coincident(g5,g1)
    c: Coincident(g5,g2)
    c: Coincident(g6,g2)
    c: Coincident(g6,g3)
    c: Horizontal(g6)
    c: Coincident(g7,g3)
    c: Coincident(g7,g0)
    c: Vertical(g7)
    c: Radius(g0) = 0.9
    c: DistanceY(g0,g0) = 0
    c: Angle(g3) = 1.5708
    c: DistanceY(g3,g3) = 0
    c: DistanceY(g3,g0) = 0.8
    c: DistanceY(g3) = 14.43
    c: Radius(g3) = 0.9
    c: Radius(g2) = 0.9
    c: Radius(g1) = 0.9
    c: DistanceX(g6,g6) = 3.6
    c: DistanceX(g3) = 12.75
    c: DistanceY(g1,g1) = 0
    c: DistanceX(g2,g2) = 0
    c: Angle(g1) = 1.5708
    c: Angle(g2) = 1.5708
    c: Vertical(g5)
    c: DistanceX(g0,g0) = 0
FEATURE [Sketcher::SketchObject] Sketch015
  FullyConstrained = true
  Placement = pos=(0,0,0) rot=(1,0,0;1.5708rad)
  sketch-geometry (8):
    g0: ArcOfCircle CenterX=11.7 CenterY=15.45 CenterZ=0 NormalX=0 NormalY=0 NormalZ=1 AngleXU=0 Radius=0.9 StartAngle=1.5708 EndAngle=3.14159
    g1: ArcOfCircle CenterX=17.4 CenterY=15.45 CenterZ=0 NormalX=0 NormalY=0 NormalZ=1 AngleXU=0 Radius=0.9 StartAngle=4e-16 EndAngle=1.5708
    g2: ArcOfCircle CenterX=16.8 CenterY=14.2 CenterZ=0 NormalX=0 NormalY=0 NormalZ=1 AngleXU=0 Radius=1.5 StartAngle=4.71239 EndAngle=6.28319
    g3: ArcOfCircle CenterX=12.3 CenterY=14.2 CenterZ=0 NormalX=0 NormalY=0 NormalZ=1 AngleXU=0 Radius=1.5 StartAngle=3.14159 EndAngle=4.71239
    g4: LineSegment StartX=11.7 StartY=16.35 StartZ=0 EndX=17.4 EndY=16.35 EndZ=0
    g5: LineSegment StartX=18.3 StartY=15.45 StartZ=0 EndX=18.3 EndY=14.2 EndZ=0
    g6: LineSegment StartX=16.8 StartY=12.7 StartZ=0 EndX=12.3 EndY=12.7 EndZ=0
    g7: LineSegment StartX=10.8 StartY=14.2 StartZ=0 EndX=10.8 EndY=15.45 EndZ=0
  constraints (28):
    c: Coincident(g4,g0)
    c: Coincident(g4,g1)
    c: Horizontal(g4)
    c: Coincident(g5,g1)
    c: Coincident(g5,g2)
    c: Coincident(g6,g2)
    c: Coincident(g6,g3)
    c: Horizontal(g6)
    c: Coincident(g7,g3)
    c: Coincident(g7,g0)
    c: Vertical(g7)
    c: Radius(g0) = 0.9
    c: DistanceY(g0,g0) = 0
    c: Angle(g3) = 1.5708
    c: DistanceY(g3,g3) = 0
    c: DistanceY(g3,g0) = 1.25
    c: DistanceY(g3) = 14.2
    c: Radius(g3) = 1.5
    c: Radius(g2) = 1.5
    c: Radius(g1) = 0.9
    c: DistanceX(g6,g6) = 4.5
    c: DistanceX(g3) = 12.3
    c: DistanceY(g1,g1) = 0
    c: DistanceX(g2,g2) = 0
    c: Angle(g1) = 1.5708
    c: Angle(g2) = 1.5708
    c: Vertical(g5)
    c: DistanceX(g0,g0) = 0
FEATURE [Part::Extrusion] Extrude014
  Base = -> Sketch014
  Dir = (0,-1,2e-16)
  DirMode = 2
  FaceMakerClass = Part::FaceMakerBullseye
  LengthFwd = 2.75
  LengthRev = 0
  Placement = pos=(0,2,0) rot=(0,0,1;0rad)
  Solid = true
  Symmetric = false
FEATURE [Part::Extrusion] Extrude015
  Base = -> Sketch015
  Dir = (0,-1,2e-16)
  DirMode = 2
  FaceMakerClass = Part::FaceMakerBullseye
  LengthFwd = 1
  LengthRev = 0
  Placement = pos=(0,2.5,0) rot=(0,0,1;0rad)
  Solid = true
  Symmetric = false
FEATURE [Part::MultiFuse] Fusion018  label="button1"
  Shapes = -> [Extrude014,Extrude015]
FEATURE [Part::MultiFuse] Fusion020  label="bottomCuts"
  Shapes = -> [Fusion017,Extrude011,Extrude004,Fusion007,Fusion001]
FEATURE [Sketcher::SketchObject] Sketch018
  FullyConstrained = true
  Placement = pos=(0,0,0) rot=(1,0,0;1.5708rad)
  sketch-geometry (8):
    g0: ArcOfCircle CenterX=11.8 CenterY=15.45 CenterZ=0 NormalX=0 NormalY=0 NormalZ=1 AngleXU=0 Radius=1.25 StartAngle=1.5708 EndAngle=3.14159
    g1: ArcOfCircle CenterX=17.3 CenterY=15.45 CenterZ=0 NormalX=0 NormalY=0 NormalZ=1 AngleXU=0 Radius=1.25 StartAngle=-9e-16 EndAngle=1.5708
    g2: ArcOfCircle CenterX=16.8 CenterY=14.2 CenterZ=0 NormalX=0 NormalY=0 NormalZ=1 AngleXU=0 Radius=1.75 StartAngle=4.71239 EndAngle=6.28319
    g3: ArcOfCircle CenterX=12.3 CenterY=14.2 CenterZ=0 NormalX=0 NormalY=0 NormalZ=1 AngleXU=0 Radius=1.75 StartAngle=3.14159 EndAngle=4.71239
    g4: LineSegment StartX=11.8 StartY=16.7 StartZ=0 EndX=17.3 EndY=16.7 EndZ=0
    g5: LineSegment StartX=18.55 StartY=15.45 StartZ=0 EndX=18.55 EndY=14.2 EndZ=0
    g6: LineSegment StartX=16.8 StartY=12.45 StartZ=0 EndX=12.3 EndY=12.45 EndZ=0
    g7: LineSegment StartX=10.55 StartY=14.2 StartZ=0 EndX=10.55 EndY=15.45 EndZ=0
  constraints (28):
    c: Coincident(g4,g0)
    c: Coincident(g4,g1)
    c: Horizontal(g4)
    c: Coincident(g5,g1)
    c: Coincident(g5,g2)
    c: Coincident(g6,g2)
    c: Coincident(g6,g3)
    c: Horizontal(g6)
    c: Coincident(g7,g3)
    c: Coincident(g7,g0)
    c: Vertical(g7)
    c: Radius(g0) = 1.25
    c: DistanceY(g0,g0) = 0
    c: Angle(g3) = 1.5708
    c: DistanceY(g3,g3) = 0
    c: DistanceY(g3,g0) = 1.25
    c: DistanceY(g3) = 14.2
    c: Radius(g3) = 1.75
    c: Radius(g2) = 1.75
    c: Radius(g1) = 1.25
    c: DistanceX(g6,g6) = 4.5
    c: DistanceX(g3) = 12.3
    c: DistanceY(g1,g1) = 0
    c: DistanceX(g2,g2) = 0
    c: Angle(g1) = 1.5708
    c: Angle(g2) = 1.5708
    c: Vertical(g5)
    c: DistanceX(g0,g0) = 0
FEATURE [Part::Extrusion] Extrude018  label="buttonCuts"
  Base = -> Sketch018
  Dir = (0,-1,2e-16)
  DirMode = 2
  FaceMakerClass = Part::FaceMakerBullseye
  LengthFwd = 0.6
  LengthRev = 0
  Placement = pos=(0,2,0) rot=(0,0,1;0rad)
  Solid = true
  Symmetric = false
FEATURE [Sketcher::SketchObject] Sketch019
  FullyConstrained = true
  Placement = pos=(0,0,0) rot=(1,0,0;1.5708rad)
  sketch-geometry (8):
    g0: ArcOfCircle CenterX=11.8 CenterY=15.45 CenterZ=0 NormalX=0 NormalY=0 NormalZ=1 AngleXU=0 Radius=1.25 StartAngle=1.5708 EndAngle=3.14159
    g1: ArcOfCircle CenterX=17.3 CenterY=15.45 CenterZ=0 NormalX=0 NormalY=0 NormalZ=1 AngleXU=0 Radius=1.25 StartAngle=-9e-16 EndAngle=1.5708
    g2: ArcOfCircle CenterX=16.8 CenterY=14.2 CenterZ=0 NormalX=0 NormalY=0 NormalZ=1 AngleXU=0 Radius=1.75 StartAngle=4.71239 EndAngle=6.28319
    g3: ArcOfCircle CenterX=12.3 CenterY=14.2 CenterZ=0 NormalX=0 NormalY=0 NormalZ=1 AngleXU=0 Radius=1.75 StartAngle=3.14159 EndAngle=4.71239
    g4: LineSegment StartX=11.8 StartY=16.7 StartZ=0 EndX=17.3 EndY=16.7 EndZ=0
    g5: LineSegment StartX=18.55 StartY=15.45 StartZ=0 EndX=18.55 EndY=14.2 EndZ=0
    g6: LineSegment StartX=16.8 StartY=12.45 StartZ=0 EndX=12.3 EndY=12.45 EndZ=0
    g7: LineSegment StartX=10.55 StartY=14.2 StartZ=0 EndX=10.55 EndY=15.45 EndZ=0
  constraints (28):
    c: Coincident(g4,g0)
    c: Coincident(g4,g1)
    c: Horizontal(g4)
    c: Coincident(g5,g1)
    c: Coincident(g5,g2)
    c: Coincident(g6,g2)
    c: Coincident(g6,g3)
    c: Horizontal(g6)
    c: Coincident(g7,g3)
    c: Coincident(g7,g0)
    c: Vertical(g7)
    c: Radius(g0) = 1.25
    c: DistanceY(g0,g0) = 0
    c: Angle(g3) = 1.5708
    c: DistanceY(g3,g3) = 0
    c: DistanceY(g3,g0) = 1.25
    c: DistanceY(g3) = 14.2
    c: Radius(g3) = 1.75
    c: Radius(g2) = 1.75
    c: Radius(g1) = 1.25
    c: DistanceX(g6,g6) = 4.5
    c: DistanceX(g3) = 12.3
    c: DistanceY(g1,g1) = 0
    c: DistanceX(g2,g2) = 0
    c: Angle(g1) = 1.5708
    c: Angle(g2) = 1.5708
    c: Vertical(g5)
    c: DistanceX(g0,g0) = 0
FEATURE [Part::Extrusion] Extrude019  label="buttonCuts001"
  Base = -> Sketch019
  Dir = (0,-1,2e-16)
  DirMode = 2
  FaceMakerClass = Part::FaceMakerBullseye
  LengthFwd = 0.6
  LengthRev = 0
  Placement = pos=(32.5,2,0) rot=(0,0,1;0rad)
  Solid = true
  Symmetric = false
FEATURE [Part::MultiFuse] Fusion022  label="buttonCuts002"
  Shapes = -> [Extrude019,Extrude018]
FEATURE [Part::MultiFuse] Fusion023  label="bottomCuts001"
  Shapes = -> [Fusion022,Fusion020]
FEATURE [Part::Cut] Cut005  label="bottom004"
  Base = -> Fusion012
  Tool = -> Fusion023
FEATURE [Part::Fillet] Fillet006  label="bottom005"
  Base = -> Cut005
  Edges = 46 edges r=0.4: [Edge107,Edge108,Edge109,Edge110,Edge139,Edge140,Edge141,Edge142,Edge172,Edge173,Edge174,Edge175,Edge176,Edge177,Edge178,Edge179,Edge180,Edge181,Edge182,Edge183,Edge184,Edge185,Edge186,Edge187,Edge188,Edge189,Edge190,Edge192,Edge194,Edge196,Edge198,Edge200,Edge202,Edge204,Edge206,Edge207,Edge208,+9 more]
FEATURE [Mesh::Feature] wearableV5_LoGo  label="wearableV5-LoGo"
  Placement = pos=(4,0,1) rot=(0,0,1;0rad)
FEATURE [Part::MultiFuse] Fusion024  label="topCuts"
  Shapes = -> [Fusion009,Part__Feature060]
FEATURE [Part::Cut] Cut006  label="top002"
  Base = -> Fusion015
  Tool = -> Fusion024
